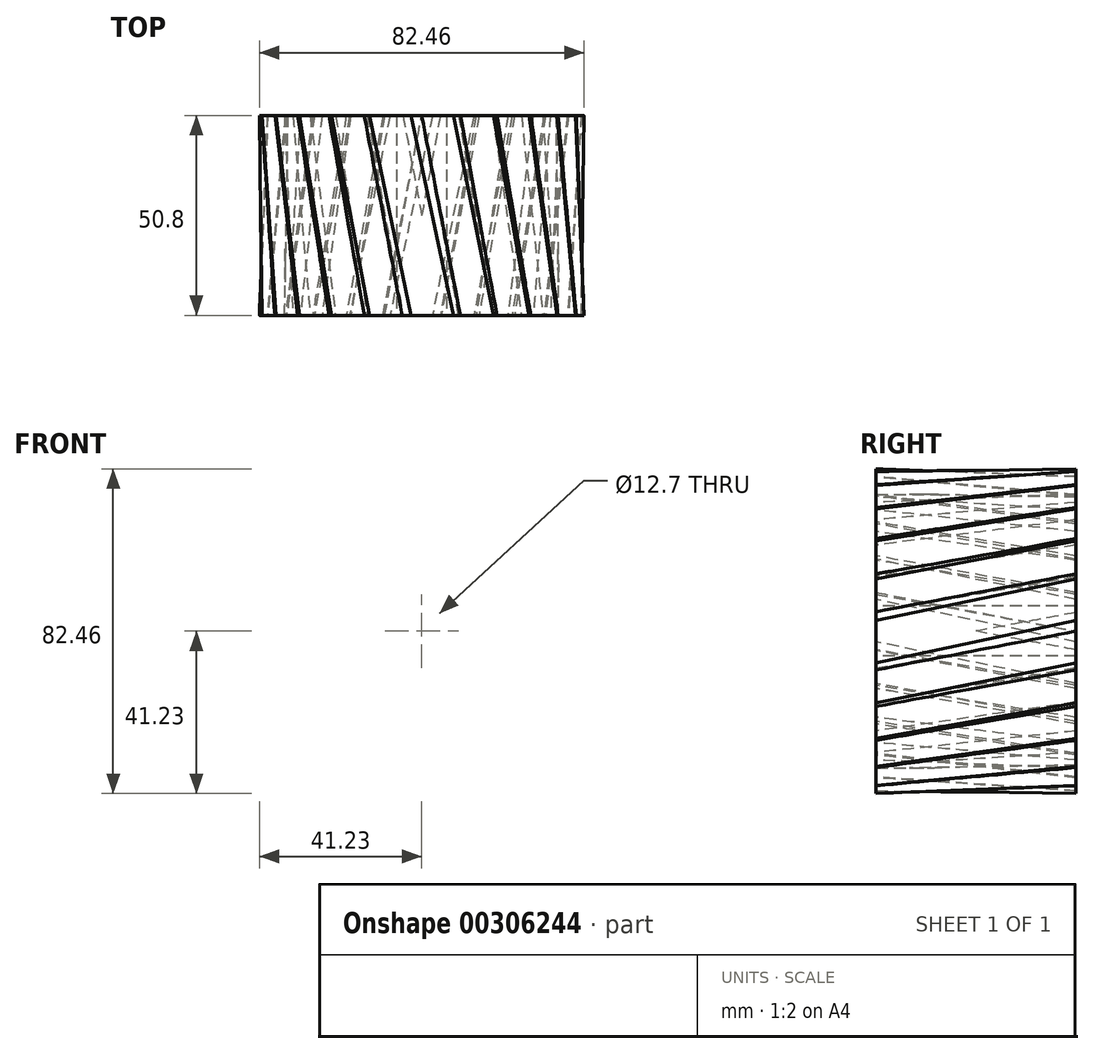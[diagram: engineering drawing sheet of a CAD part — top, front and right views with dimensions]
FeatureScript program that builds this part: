
annotation { "Feature Type Name" : "Feature", "Feature Type Description" : "" }
export const myFeature = defineFeature(function(context is Context, id is Id, definition is map)
    precondition{}
    {
        {
            var Q0;
            Q0=qCreatedBy(makeId("Front.planeOp"),FACE);
            cPlane(context, id + "F0", {"entities" : qUnion([Q0]), "cplaneType" : CPlaneType.OFFSET, "offset" : 50.8 * mm, "width" : 152.4 * mm, "height" : 152.4 * mm});
        }
        {
            var Q0;
            Q0=qCreatedBy(makeId("Front.planeOp"),FACE);
            var sketch = newSketch(context, id + "F1", { "sketchPlane" : qUnion([Q0])});
            skArc(sketch, "E0", {"start": v(-6.06, 34.4) * mm, "mid": v(-6.81, 34.25) * mm, "end": v(-7.56, 34.1) * mm});
            skArc(sketch, "E1.trimOffspring", {"start": v(-0.13, 38.41) * mm, "mid": v(-0.86, 39.8) * mm, "end": v(-1.82, 41.06) * mm});
            skLineSegment(sketch, "E2", {"start": v(0, 37.8) * mm, "end": v(0, 36.48) * mm});
            skLineSegment(sketch, "E3", {"start": v(-2.2, 41.23) * mm, "end": v(-2.7, 41.23) * mm});
            skLineSegment(sketch, "E4.MirrorCS", {"start": v(-3.2, 41.16) * mm, "end": v(-2.7, 41.23) * mm});
            skArc(sketch, "E5.MirrorCS", {"start": v(-4.89, 38.1) * mm, "mid": v(-4.34, 39.58) * mm, "end": v(-3.56, 40.95) * mm});
            skLineSegment(sketch, "E6.MirrorCS", {"start": v(-4.93, 37.47) * mm, "end": v(-4.76, 36.17) * mm});
            skPoint(sketch, "E7.visualSharp", {"position": v(0, 34.93) * mm});
            skArc(sketch, "E7.filletArc", {"start": v(0, 35.2) * mm, "mid": v(0.08, 35) * mm, "end": v(0.28, 34.92) * mm});
            skArc(sketch, "E8.filletArc", {"start": v(0, 36.48) * mm, "mid": v(0.44, 35.38) * mm, "end": v(1.52, 34.9) * mm});
            skPoint(sketch, "E9.visualSharp", {"position": v(-4.56, 34.63) * mm});
            skArc(sketch, "E9.filletArc", {"start": v(-6.06, 34.4) * mm, "mid": v(-5.06, 35.02) * mm, "end": v(-4.76, 36.17) * mm});
            skPoint(sketch, "E10.visualSharp", {"position": v(-4.97, 37.77) * mm});
            skArc(sketch, "E10.filletArc", {"start": v(-4.89, 38.1) * mm, "mid": v(-4.94, 37.79) * mm, "end": v(-4.93, 37.47) * mm});
            skPoint(sketch, "E11.visualSharp", {"position": v(0, 38.1) * mm});
            skArc(sketch, "E11.filletArc", {"start": v(0, 37.8) * mm, "mid": v(-0.03, 38.1) * mm, "end": v(-0.13, 38.41) * mm});
            skPoint(sketch, "E12.visualSharp", {"position": v(-3.43, 41.13) * mm});
            skArc(sketch, "E12.filletArc", {"start": v(-3.2, 41.16) * mm, "mid": v(-3.4, 41.1) * mm, "end": v(-3.56, 40.95) * mm});
            skPoint(sketch, "E13.visualSharp", {"position": v(-1.97, 41.23) * mm});
            skArc(sketch, "E13.filletArc", {"start": v(-1.82, 41.06) * mm, "mid": v(-1.99, 41.18) * mm, "end": v(-2.2, 41.23) * mm});
            skArc(sketch, "E14.1.0", {"start": v(-9.44, 35.24) * mm, "mid": v(-8.73, 34.29) * mm, "end": v(-7.56, 34.1) * mm});
            skLineSegment(sketch, "E14.1.1", {"start": v(-9.78, 36.5) * mm, "end": v(-9.44, 35.24) * mm});
            skLineSegment(sketch, "E14.1.2", {"start": v(-14.46, 34.91) * mm, "end": v(-13.96, 33.7) * mm});
            skLineSegment(sketch, "E14.1.3", {"start": v(-12.79, 39.26) * mm, "end": v(-13.28, 39.12) * mm});
            skPoint(sketch, "E14.1.4", {"position": v(-12.58, 39.31) * mm});
            skPoint(sketch, "E14.1.5", {"position": v(-13.96, 38.84) * mm});
            skLineSegment(sketch, "E14.1.6", {"start": v(-13.75, 38.93) * mm, "end": v(-13.28, 39.12) * mm});
            skArc(sketch, "E14.1.7", {"start": v(-10.06, 37.07) * mm, "mid": v(-11.14, 38.23) * mm, "end": v(-12.38, 39.2) * mm});
            skPoint(sketch, "E14.1.8", {"position": v(-9.86, 36.8) * mm});
            skArc(sketch, "E14.1.9", {"start": v(-14.58, 35.54) * mm, "mid": v(-14.44, 37.1) * mm, "end": v(-14.03, 38.63) * mm});
            skPoint(sketch, "E14.1.10", {"position": v(-14.58, 35.2) * mm});
            skArc(sketch, "E14.1.11", {"start": v(-14.58, 35.54) * mm, "mid": v(-14.55, 35.22) * mm, "end": v(-14.46, 34.91) * mm});
            skArc(sketch, "E14.1.12", {"start": v(-9.78, 36.5) * mm, "mid": v(-9.9, 36.8) * mm, "end": v(-10.06, 37.07) * mm});
            skArc(sketch, "E14.1.13", {"start": v(-12.38, 39.2) * mm, "mid": v(-12.58, 39.27) * mm, "end": v(-12.79, 39.26) * mm});
            skArc(sketch, "E14.1.14", {"start": v(-13.75, 38.93) * mm, "mid": v(-13.92, 38.8) * mm, "end": v(-14.03, 38.63) * mm});
            skArc(sketch, "E14.1.15", {"start": v(-14.76, 31.65) * mm, "mid": v(-13.95, 32.52) * mm, "end": v(-13.96, 33.7) * mm});
            skArc(sketch, "E14.2.0", {"start": v(-18.24, 31.6) * mm, "mid": v(-17.3, 30.86) * mm, "end": v(-16.13, 30.98) * mm});
            skLineSegment(sketch, "E14.2.1", {"start": v(-18.9, 32.73) * mm, "end": v(-18.24, 31.6) * mm});
            skLineSegment(sketch, "E14.2.2", {"start": v(-23, 29.98) * mm, "end": v(-22.2, 28.94) * mm});
            skLineSegment(sketch, "E14.2.3", {"start": v(-22.51, 34.6) * mm, "end": v(-22.95, 34.35) * mm});
            skPoint(sketch, "E14.2.4", {"position": v(-22.32, 34.72) * mm});
            skPoint(sketch, "E14.2.5", {"position": v(-23.53, 33.9) * mm});
            skLineSegment(sketch, "E14.2.6", {"start": v(-23.36, 34.04) * mm, "end": v(-22.95, 34.35) * mm});
            skArc(sketch, "E14.2.7", {"start": v(-19.32, 33.2) * mm, "mid": v(-20.65, 34.04) * mm, "end": v(-22.1, 34.65) * mm});
            skPoint(sketch, "E14.2.8", {"position": v(-19.05, 33) * mm});
            skArc(sketch, "E14.2.9", {"start": v(-23.28, 30.55) * mm, "mid": v(-23.55, 32.1) * mm, "end": v(-23.55, 33.68) * mm});
            skPoint(sketch, "E14.2.10", {"position": v(-23.2, 30.23) * mm});
            skArc(sketch, "E14.2.11", {"start": v(-23.28, 30.55) * mm, "mid": v(-23.17, 30.25) * mm, "end": v(-23, 29.98) * mm});
            skArc(sketch, "E14.2.12", {"start": v(-18.9, 32.73) * mm, "mid": v(-19.08, 32.99) * mm, "end": v(-19.32, 33.2) * mm});
            skArc(sketch, "E14.2.13", {"start": v(-22.1, 34.65) * mm, "mid": v(-22.31, 34.67) * mm, "end": v(-22.51, 34.6) * mm});
            skArc(sketch, "E14.2.14", {"start": v(-23.36, 34.04) * mm, "mid": v(-23.5, 33.88) * mm, "end": v(-23.55, 33.68) * mm});
            skArc(sketch, "E14.2.15", {"start": v(-22.45, 26.76) * mm, "mid": v(-21.89, 27.8) * mm, "end": v(-22.2, 28.94) * mm});
            skArc(sketch, "E15.3.3.0", {"start": v(-25.8, 25.8) * mm, "mid": v(-24.7, 25.33) * mm, "end": v(-23.6, 25.75) * mm});
            skLineSegment(sketch, "E15.4.3.0", {"start": v(-26.72, 26.72) * mm, "end": v(-25.8, 25.8) * mm});
            skLineSegment(sketch, "E15.7.3.0", {"start": v(-29.98, 23) * mm, "end": v(-28.94, 22.2) * mm});
            skLineSegment(sketch, "E15.10.3.0", {"start": v(-30.7, 27.6) * mm, "end": v(-31.06, 27.24) * mm});
            skPoint(sketch, "E15.13.3.0", {"position": v(-30.55, 27.76) * mm});
            skPoint(sketch, "E15.14.3.0", {"position": v(-31.5, 26.66) * mm});
            skLineSegment(sketch, "E15.15.3.0", {"start": v(-31.37, 26.84) * mm, "end": v(-31.06, 27.24) * mm});
            skArc(sketch, "E15.18.3.0", {"start": v(-27.25, 27.07) * mm, "mid": v(-28.76, 27.54) * mm, "end": v(-30.32, 27.75) * mm});
            skPoint(sketch, "E15.22.3.0", {"position": v(-26.94, 26.94) * mm});
            skArc(sketch, "E15.23.3.0", {"start": v(-30.4, 23.49) * mm, "mid": v(-31.06, 24.92) * mm, "end": v(-31.47, 26.44) * mm});
            skPoint(sketch, "E15.27.3.0", {"position": v(-30.23, 23.2) * mm});
            skArc(sketch, "E15.28.3.0", {"start": v(-30.4, 23.49) * mm, "mid": v(-30.21, 23.22) * mm, "end": v(-29.98, 23) * mm});
            skArc(sketch, "E15.32.3.0", {"start": v(-26.72, 26.72) * mm, "mid": v(-26.97, 26.92) * mm, "end": v(-27.25, 27.07) * mm});
            skArc(sketch, "E15.36.3.0", {"start": v(-30.32, 27.75) * mm, "mid": v(-30.53, 27.72) * mm, "end": v(-30.7, 27.6) * mm});
            skArc(sketch, "E15.40.3.0", {"start": v(-31.37, 26.84) * mm, "mid": v(-31.46, 26.65) * mm, "end": v(-31.47, 26.44) * mm});
            skArc(sketch, "E15.44.3.0", {"start": v(-28.6, 20.04) * mm, "mid": v(-28.34, 21.19) * mm, "end": v(-28.94, 22.2) * mm});
            skArc(sketch, "E15.3.4.0", {"start": v(-31.6, 18.24) * mm, "mid": v(-30.42, 18.07) * mm, "end": v(-29.46, 18.76) * mm});
            skLineSegment(sketch, "E15.4.4.0", {"start": v(-32.73, 18.9) * mm, "end": v(-31.6, 18.24) * mm});
            skLineSegment(sketch, "E15.7.4.0", {"start": v(-34.91, 14.46) * mm, "end": v(-33.7, 13.96) * mm});
            skLineSegment(sketch, "E15.10.4.0", {"start": v(-36.8, 18.71) * mm, "end": v(-37.06, 18.27) * mm});
            skPoint(sketch, "E15.13.4.0", {"position": v(-36.7, 18.9) * mm});
            skPoint(sketch, "E15.14.4.0", {"position": v(-37.33, 17.6) * mm});
            skLineSegment(sketch, "E15.15.4.0", {"start": v(-37.25, 17.8) * mm, "end": v(-37.06, 18.27) * mm});
            skArc(sketch, "E15.18.4.0", {"start": v(-33.33, 19.1) * mm, "mid": v(-34.9, 19.16) * mm, "end": v(-36.47, 18.96) * mm});
            skPoint(sketch, "E15.22.4.0", {"position": v(-33, 19.05) * mm});
            skArc(sketch, "E15.23.4.0", {"start": v(-35.44, 14.82) * mm, "mid": v(-36.45, 16.03) * mm, "end": v(-37.24, 17.4) * mm});
            skPoint(sketch, "E15.27.4.0", {"position": v(-35.2, 14.58) * mm});
            skArc(sketch, "E15.28.4.0", {"start": v(-35.44, 14.82) * mm, "mid": v(-35.2, 14.61) * mm, "end": v(-34.91, 14.46) * mm});
            skArc(sketch, "E15.32.4.0", {"start": v(-32.73, 18.9) * mm, "mid": v(-33.02, 19.03) * mm, "end": v(-33.33, 19.1) * mm});
            skArc(sketch, "E15.36.4.0", {"start": v(-36.47, 18.96) * mm, "mid": v(-36.66, 18.87) * mm, "end": v(-36.8, 18.71) * mm});
            skArc(sketch, "E15.40.4.0", {"start": v(-37.25, 17.8) * mm, "mid": v(-37.29, 17.6) * mm, "end": v(-37.24, 17.4) * mm});
            skArc(sketch, "E15.44.4.0", {"start": v(-32.82, 11.95) * mm, "mid": v(-32.86, 13.13) * mm, "end": v(-33.7, 13.96) * mm});
            skArc(sketch, "E15.3.5.0", {"start": v(-35.24, 9.44) * mm, "mid": v(-34.06, 9.58) * mm, "end": v(-33.31, 10.5) * mm});
            skLineSegment(sketch, "E15.4.5.0", {"start": v(-36.5, 9.78) * mm, "end": v(-35.24, 9.44) * mm});
            skLineSegment(sketch, "E15.7.5.0", {"start": v(-37.47, 4.93) * mm, "end": v(-36.17, 4.76) * mm});
            skLineSegment(sketch, "E15.10.5.0", {"start": v(-40.4, 8.55) * mm, "end": v(-40.52, 8.06) * mm});
            skPoint(sketch, "E15.13.5.0", {"position": v(-40.33, 8.77) * mm});
            skPoint(sketch, "E15.14.5.0", {"position": v(-40.62, 7.34) * mm});
            skLineSegment(sketch, "E15.15.5.0", {"start": v(-40.59, 7.56) * mm, "end": v(-40.52, 8.06) * mm});
            skArc(sketch, "E15.18.5.0", {"start": v(-37.14, 9.82) * mm, "mid": v(-38.67, 9.47) * mm, "end": v(-40.13, 8.87) * mm});
            skPoint(sketch, "E15.22.5.0", {"position": v(-36.8, 9.86) * mm});
            skArc(sketch, "E15.23.5.0", {"start": v(-38.07, 5.14) * mm, "mid": v(-39.35, 6.05) * mm, "end": v(-40.47, 7.16) * mm});
            skPoint(sketch, "E15.27.5.0", {"position": v(-37.77, 4.97) * mm});
            skArc(sketch, "E15.28.5.0", {"start": v(-38.07, 5.14) * mm, "mid": v(-37.78, 5) * mm, "end": v(-37.47, 4.93) * mm});
            skArc(sketch, "E15.32.5.0", {"start": v(-36.5, 9.78) * mm, "mid": v(-36.82, 9.83) * mm, "end": v(-37.14, 9.82) * mm});
            skArc(sketch, "E15.36.5.0", {"start": v(-40.13, 8.87) * mm, "mid": v(-40.3, 8.74) * mm, "end": v(-40.4, 8.55) * mm});
            skArc(sketch, "E15.40.5.0", {"start": v(-40.59, 7.56) * mm, "mid": v(-40.57, 7.35) * mm, "end": v(-40.47, 7.16) * mm});
            skArc(sketch, "E15.44.5.0", {"start": v(-34.8, 3.05) * mm, "mid": v(-35.13, 4.18) * mm, "end": v(-36.17, 4.76) * mm});
            skArc(sketch, "E15.3.6.0", {"start": v(-36.48, 0) * mm, "mid": v(-35.38, 0.44) * mm, "end": v(-34.9, 1.52) * mm});
            skLineSegment(sketch, "E15.4.6.0", {"start": v(-37.8, 0) * mm, "end": v(-36.48, 0) * mm});
            skLineSegment(sketch, "E15.7.6.0", {"start": v(-37.47, -4.93) * mm, "end": v(-36.17, -4.76) * mm});
            skLineSegment(sketch, "E15.10.6.0", {"start": v(-41.23, -2.2) * mm, "end": v(-41.23, -2.7) * mm});
            skPoint(sketch, "E15.13.6.0", {"position": v(-41.23, -1.97) * mm});
            skPoint(sketch, "E15.14.6.0", {"position": v(-41.13, -3.43) * mm});
            skLineSegment(sketch, "E15.15.6.0", {"start": v(-41.16, -3.2) * mm, "end": v(-41.23, -2.7) * mm});
            skArc(sketch, "E15.18.6.0", {"start": v(-38.41, -0.13) * mm, "mid": v(-39.8, -0.86) * mm, "end": v(-41.06, -1.82) * mm});
            skPoint(sketch, "E15.22.6.0", {"position": v(-38.1, 0) * mm});
            skArc(sketch, "E15.23.6.0", {"start": v(-38.1, -4.89) * mm, "mid": v(-39.58, -4.34) * mm, "end": v(-40.95, -3.56) * mm});
            skPoint(sketch, "E15.27.6.0", {"position": v(-37.77, -4.97) * mm});
            skArc(sketch, "E15.28.6.0", {"start": v(-38.1, -4.89) * mm, "mid": v(-37.79, -4.94) * mm, "end": v(-37.47, -4.93) * mm});
            skArc(sketch, "E15.32.6.0", {"start": v(-37.8, 0) * mm, "mid": v(-38.1, -0.03) * mm, "end": v(-38.41, -0.13) * mm});
            skArc(sketch, "E15.36.6.0", {"start": v(-41.06, -1.82) * mm, "mid": v(-41.18, -1.99) * mm, "end": v(-41.23, -2.2) * mm});
            skArc(sketch, "E15.40.6.0", {"start": v(-41.16, -3.2) * mm, "mid": v(-41.1, -3.4) * mm, "end": v(-40.95, -3.56) * mm});
            skArc(sketch, "E15.44.6.0", {"start": v(-34.4, -6.06) * mm, "mid": v(-35.02, -5.06) * mm, "end": v(-36.17, -4.76) * mm});
            skArc(sketch, "E15.3.7.0", {"start": v(-35.24, -9.44) * mm, "mid": v(-34.29, -8.73) * mm, "end": v(-34.1, -7.56) * mm});
            skLineSegment(sketch, "E15.4.7.0", {"start": v(-36.5, -9.78) * mm, "end": v(-35.24, -9.44) * mm});
            skLineSegment(sketch, "E15.7.7.0", {"start": v(-34.91, -14.46) * mm, "end": v(-33.7, -13.96) * mm});
            skLineSegment(sketch, "E15.10.7.0", {"start": v(-39.26, -12.79) * mm, "end": v(-39.12, -13.28) * mm});
            skPoint(sketch, "E15.13.7.0", {"position": v(-39.31, -12.58) * mm});
            skPoint(sketch, "E15.14.7.0", {"position": v(-38.84, -13.96) * mm});
            skLineSegment(sketch, "E15.15.7.0", {"start": v(-38.93, -13.75) * mm, "end": v(-39.12, -13.28) * mm});
            skArc(sketch, "E15.18.7.0", {"start": v(-37.07, -10.06) * mm, "mid": v(-38.23, -11.14) * mm, "end": v(-39.2, -12.38) * mm});
            skPoint(sketch, "E15.22.7.0", {"position": v(-36.8, -9.86) * mm});
            skArc(sketch, "E15.23.7.0", {"start": v(-35.54, -14.58) * mm, "mid": v(-37.1, -14.44) * mm, "end": v(-38.63, -14.03) * mm});
            skPoint(sketch, "E15.27.7.0", {"position": v(-35.2, -14.58) * mm});
            skArc(sketch, "E15.28.7.0", {"start": v(-35.54, -14.58) * mm, "mid": v(-35.22, -14.55) * mm, "end": v(-34.91, -14.46) * mm});
            skArc(sketch, "E15.32.7.0", {"start": v(-36.5, -9.78) * mm, "mid": v(-36.8, -9.9) * mm, "end": v(-37.07, -10.06) * mm});
            skArc(sketch, "E15.36.7.0", {"start": v(-39.2, -12.38) * mm, "mid": v(-39.27, -12.58) * mm, "end": v(-39.26, -12.79) * mm});
            skArc(sketch, "E15.40.7.0", {"start": v(-38.93, -13.75) * mm, "mid": v(-38.8, -13.92) * mm, "end": v(-38.63, -14.03) * mm});
            skArc(sketch, "E15.44.7.0", {"start": v(-31.65, -14.76) * mm, "mid": v(-32.52, -13.95) * mm, "end": v(-33.7, -13.96) * mm});
            skArc(sketch, "E15.3.8.0", {"start": v(-31.6, -18.24) * mm, "mid": v(-30.86, -17.3) * mm, "end": v(-30.98, -16.13) * mm});
            skLineSegment(sketch, "E15.4.8.0", {"start": v(-32.73, -18.9) * mm, "end": v(-31.6, -18.24) * mm});
            skLineSegment(sketch, "E15.7.8.0", {"start": v(-29.98, -23) * mm, "end": v(-28.94, -22.2) * mm});
            skLineSegment(sketch, "E15.10.8.0", {"start": v(-34.6, -22.51) * mm, "end": v(-34.35, -22.95) * mm});
            skPoint(sketch, "E15.13.8.0", {"position": v(-34.72, -22.32) * mm});
            skPoint(sketch, "E15.14.8.0", {"position": v(-33.9, -23.53) * mm});
            skLineSegment(sketch, "E15.15.8.0", {"start": v(-34.04, -23.36) * mm, "end": v(-34.35, -22.95) * mm});
            skArc(sketch, "E15.18.8.0", {"start": v(-33.2, -19.32) * mm, "mid": v(-34.04, -20.65) * mm, "end": v(-34.65, -22.1) * mm});
            skPoint(sketch, "E15.22.8.0", {"position": v(-33, -19.05) * mm});
            skArc(sketch, "E15.23.8.0", {"start": v(-30.55, -23.28) * mm, "mid": v(-32.1, -23.55) * mm, "end": v(-33.68, -23.55) * mm});
            skPoint(sketch, "E15.27.8.0", {"position": v(-30.23, -23.2) * mm});
            skArc(sketch, "E15.28.8.0", {"start": v(-30.55, -23.28) * mm, "mid": v(-30.25, -23.17) * mm, "end": v(-29.98, -23) * mm});
            skArc(sketch, "E15.32.8.0", {"start": v(-32.73, -18.9) * mm, "mid": v(-32.99, -19.08) * mm, "end": v(-33.2, -19.32) * mm});
            skArc(sketch, "E15.36.8.0", {"start": v(-34.65, -22.1) * mm, "mid": v(-34.67, -22.31) * mm, "end": v(-34.6, -22.51) * mm});
            skArc(sketch, "E15.40.8.0", {"start": v(-34.04, -23.36) * mm, "mid": v(-33.88, -23.5) * mm, "end": v(-33.68, -23.55) * mm});
            skArc(sketch, "E15.44.8.0", {"start": v(-26.76, -22.45) * mm, "mid": v(-27.8, -21.89) * mm, "end": v(-28.94, -22.2) * mm});
            skArc(sketch, "E15.3.9.0", {"start": v(-25.8, -25.8) * mm, "mid": v(-25.33, -24.7) * mm, "end": v(-25.75, -23.6) * mm});
            skLineSegment(sketch, "E15.4.9.0", {"start": v(-26.72, -26.72) * mm, "end": v(-25.8, -25.8) * mm});
            skLineSegment(sketch, "E15.7.9.0", {"start": v(-23, -29.98) * mm, "end": v(-22.2, -28.94) * mm});
            skLineSegment(sketch, "E15.10.9.0", {"start": v(-27.6, -30.7) * mm, "end": v(-27.24, -31.06) * mm});
            skPoint(sketch, "E15.13.9.0", {"position": v(-27.76, -30.55) * mm});
            skPoint(sketch, "E15.14.9.0", {"position": v(-26.66, -31.5) * mm});
            skLineSegment(sketch, "E15.15.9.0", {"start": v(-26.84, -31.37) * mm, "end": v(-27.24, -31.06) * mm});
            skArc(sketch, "E15.18.9.0", {"start": v(-27.07, -27.25) * mm, "mid": v(-27.54, -28.76) * mm, "end": v(-27.75, -30.32) * mm});
            skPoint(sketch, "E15.22.9.0", {"position": v(-26.94, -26.94) * mm});
            skArc(sketch, "E15.23.9.0", {"start": v(-23.49, -30.4) * mm, "mid": v(-24.92, -31.06) * mm, "end": v(-26.44, -31.47) * mm});
            skPoint(sketch, "E15.27.9.0", {"position": v(-23.2, -30.23) * mm});
            skArc(sketch, "E15.28.9.0", {"start": v(-23.49, -30.4) * mm, "mid": v(-23.22, -30.21) * mm, "end": v(-23, -29.98) * mm});
            skArc(sketch, "E15.32.9.0", {"start": v(-26.72, -26.72) * mm, "mid": v(-26.92, -26.97) * mm, "end": v(-27.07, -27.25) * mm});
            skArc(sketch, "E15.36.9.0", {"start": v(-27.75, -30.32) * mm, "mid": v(-27.72, -30.53) * mm, "end": v(-27.6, -30.7) * mm});
            skArc(sketch, "E15.40.9.0", {"start": v(-26.84, -31.37) * mm, "mid": v(-26.65, -31.46) * mm, "end": v(-26.44, -31.47) * mm});
            skArc(sketch, "E15.44.9.0", {"start": v(-20.04, -28.6) * mm, "mid": v(-21.19, -28.34) * mm, "end": v(-22.2, -28.94) * mm});
            skArc(sketch, "E15.3.10.0", {"start": v(-18.24, -31.6) * mm, "mid": v(-18.07, -30.42) * mm, "end": v(-18.76, -29.46) * mm});
            skLineSegment(sketch, "E15.4.10.0", {"start": v(-18.9, -32.73) * mm, "end": v(-18.24, -31.6) * mm});
            skLineSegment(sketch, "E15.7.10.0", {"start": v(-14.46, -34.91) * mm, "end": v(-13.96, -33.7) * mm});
            skLineSegment(sketch, "E15.10.10.0", {"start": v(-18.71, -36.8) * mm, "end": v(-18.27, -37.06) * mm});
            skPoint(sketch, "E15.13.10.0", {"position": v(-18.9, -36.7) * mm});
            skPoint(sketch, "E15.14.10.0", {"position": v(-17.6, -37.33) * mm});
            skLineSegment(sketch, "E15.15.10.0", {"start": v(-17.8, -37.25) * mm, "end": v(-18.27, -37.06) * mm});
            skArc(sketch, "E15.18.10.0", {"start": v(-19.1, -33.33) * mm, "mid": v(-19.16, -34.9) * mm, "end": v(-18.96, -36.47) * mm});
            skPoint(sketch, "E15.22.10.0", {"position": v(-19.05, -33) * mm});
            skArc(sketch, "E15.23.10.0", {"start": v(-14.82, -35.44) * mm, "mid": v(-16.03, -36.45) * mm, "end": v(-17.4, -37.24) * mm});
            skPoint(sketch, "E15.27.10.0", {"position": v(-14.58, -35.2) * mm});
            skArc(sketch, "E15.28.10.0", {"start": v(-14.82, -35.44) * mm, "mid": v(-14.61, -35.2) * mm, "end": v(-14.46, -34.91) * mm});
            skArc(sketch, "E15.32.10.0", {"start": v(-18.9, -32.73) * mm, "mid": v(-19.03, -33.02) * mm, "end": v(-19.1, -33.33) * mm});
            skArc(sketch, "E15.36.10.0", {"start": v(-18.96, -36.47) * mm, "mid": v(-18.87, -36.66) * mm, "end": v(-18.71, -36.8) * mm});
            skArc(sketch, "E15.40.10.0", {"start": v(-17.8, -37.25) * mm, "mid": v(-17.6, -37.29) * mm, "end": v(-17.4, -37.24) * mm});
            skArc(sketch, "E15.44.10.0", {"start": v(-11.95, -32.82) * mm, "mid": v(-13.13, -32.86) * mm, "end": v(-13.96, -33.7) * mm});
            skArc(sketch, "E15.3.11.0", {"start": v(-9.44, -35.24) * mm, "mid": v(-9.58, -34.06) * mm, "end": v(-10.5, -33.31) * mm});
            skLineSegment(sketch, "E15.4.11.0", {"start": v(-9.78, -36.5) * mm, "end": v(-9.44, -35.24) * mm});
            skLineSegment(sketch, "E15.7.11.0", {"start": v(-4.93, -37.47) * mm, "end": v(-4.76, -36.17) * mm});
            skLineSegment(sketch, "E15.10.11.0", {"start": v(-8.55, -40.4) * mm, "end": v(-8.06, -40.52) * mm});
            skPoint(sketch, "E15.13.11.0", {"position": v(-8.77, -40.33) * mm});
            skPoint(sketch, "E15.14.11.0", {"position": v(-7.34, -40.62) * mm});
            skLineSegment(sketch, "E15.15.11.0", {"start": v(-7.56, -40.59) * mm, "end": v(-8.06, -40.52) * mm});
            skArc(sketch, "E15.18.11.0", {"start": v(-9.82, -37.14) * mm, "mid": v(-9.47, -38.67) * mm, "end": v(-8.87, -40.13) * mm});
            skPoint(sketch, "E15.22.11.0", {"position": v(-9.86, -36.8) * mm});
            skArc(sketch, "E15.23.11.0", {"start": v(-5.14, -38.07) * mm, "mid": v(-6.05, -39.35) * mm, "end": v(-7.16, -40.47) * mm});
            skPoint(sketch, "E15.27.11.0", {"position": v(-4.97, -37.77) * mm});
            skArc(sketch, "E15.28.11.0", {"start": v(-5.14, -38.07) * mm, "mid": v(-5, -37.78) * mm, "end": v(-4.93, -37.47) * mm});
            skArc(sketch, "E15.32.11.0", {"start": v(-9.78, -36.5) * mm, "mid": v(-9.83, -36.82) * mm, "end": v(-9.82, -37.14) * mm});
            skArc(sketch, "E15.36.11.0", {"start": v(-8.87, -40.13) * mm, "mid": v(-8.74, -40.3) * mm, "end": v(-8.55, -40.4) * mm});
            skArc(sketch, "E15.40.11.0", {"start": v(-7.56, -40.59) * mm, "mid": v(-7.35, -40.57) * mm, "end": v(-7.16, -40.47) * mm});
            skArc(sketch, "E15.44.11.0", {"start": v(-3.05, -34.8) * mm, "mid": v(-4.18, -35.13) * mm, "end": v(-4.76, -36.17) * mm});
            skArc(sketch, "E15.3.12.0", {"start": v(0, -36.48) * mm, "mid": v(-0.44, -35.38) * mm, "end": v(-1.52, -34.9) * mm});
            skLineSegment(sketch, "E15.4.12.0", {"start": v(0, -37.8) * mm, "end": v(0, -36.48) * mm});
            skLineSegment(sketch, "E15.7.12.0", {"start": v(4.93, -37.47) * mm, "end": v(4.76, -36.17) * mm});
            skLineSegment(sketch, "E15.10.12.0", {"start": v(2.2, -41.23) * mm, "end": v(2.7, -41.23) * mm});
            skPoint(sketch, "E15.13.12.0", {"position": v(1.97, -41.23) * mm});
            skPoint(sketch, "E15.14.12.0", {"position": v(3.43, -41.13) * mm});
            skLineSegment(sketch, "E15.15.12.0", {"start": v(3.2, -41.16) * mm, "end": v(2.7, -41.23) * mm});
            skArc(sketch, "E15.18.12.0", {"start": v(0.13, -38.41) * mm, "mid": v(0.86, -39.8) * mm, "end": v(1.82, -41.06) * mm});
            skPoint(sketch, "E15.22.12.0", {"position": v(0, -38.1) * mm});
            skArc(sketch, "E15.23.12.0", {"start": v(4.89, -38.1) * mm, "mid": v(4.34, -39.58) * mm, "end": v(3.56, -40.95) * mm});
            skPoint(sketch, "E15.27.12.0", {"position": v(4.97, -37.77) * mm});
            skArc(sketch, "E15.28.12.0", {"start": v(4.89, -38.1) * mm, "mid": v(4.94, -37.79) * mm, "end": v(4.93, -37.47) * mm});
            skArc(sketch, "E15.32.12.0", {"start": v(0, -37.8) * mm, "mid": v(0.03, -38.1) * mm, "end": v(0.13, -38.41) * mm});
            skArc(sketch, "E15.36.12.0", {"start": v(1.82, -41.06) * mm, "mid": v(1.99, -41.18) * mm, "end": v(2.2, -41.23) * mm});
            skArc(sketch, "E15.40.12.0", {"start": v(3.2, -41.16) * mm, "mid": v(3.4, -41.1) * mm, "end": v(3.56, -40.95) * mm});
            skArc(sketch, "E15.44.12.0", {"start": v(6.06, -34.4) * mm, "mid": v(5.06, -35.02) * mm, "end": v(4.76, -36.17) * mm});
            skArc(sketch, "E15.3.13.0", {"start": v(9.44, -35.24) * mm, "mid": v(8.73, -34.29) * mm, "end": v(7.56, -34.1) * mm});
            skLineSegment(sketch, "E15.4.13.0", {"start": v(9.78, -36.5) * mm, "end": v(9.44, -35.24) * mm});
            skLineSegment(sketch, "E15.7.13.0", {"start": v(14.46, -34.91) * mm, "end": v(13.96, -33.7) * mm});
            skLineSegment(sketch, "E15.10.13.0", {"start": v(12.79, -39.26) * mm, "end": v(13.28, -39.12) * mm});
            skPoint(sketch, "E15.13.13.0", {"position": v(12.58, -39.31) * mm});
            skPoint(sketch, "E15.14.13.0", {"position": v(13.96, -38.84) * mm});
            skLineSegment(sketch, "E15.15.13.0", {"start": v(13.75, -38.93) * mm, "end": v(13.28, -39.12) * mm});
            skArc(sketch, "E15.18.13.0", {"start": v(10.06, -37.07) * mm, "mid": v(11.14, -38.23) * mm, "end": v(12.38, -39.2) * mm});
            skPoint(sketch, "E15.22.13.0", {"position": v(9.86, -36.8) * mm});
            skArc(sketch, "E15.23.13.0", {"start": v(14.58, -35.54) * mm, "mid": v(14.44, -37.1) * mm, "end": v(14.03, -38.63) * mm});
            skPoint(sketch, "E15.27.13.0", {"position": v(14.58, -35.2) * mm});
            skArc(sketch, "E15.28.13.0", {"start": v(14.58, -35.54) * mm, "mid": v(14.55, -35.22) * mm, "end": v(14.46, -34.91) * mm});
            skArc(sketch, "E15.32.13.0", {"start": v(9.78, -36.5) * mm, "mid": v(9.9, -36.8) * mm, "end": v(10.06, -37.07) * mm});
            skArc(sketch, "E15.36.13.0", {"start": v(12.38, -39.2) * mm, "mid": v(12.58, -39.27) * mm, "end": v(12.79, -39.26) * mm});
            skArc(sketch, "E15.40.13.0", {"start": v(13.75, -38.93) * mm, "mid": v(13.92, -38.8) * mm, "end": v(14.03, -38.63) * mm});
            skArc(sketch, "E15.44.13.0", {"start": v(14.76, -31.65) * mm, "mid": v(13.95, -32.52) * mm, "end": v(13.96, -33.7) * mm});
            skArc(sketch, "E15.3.14.0", {"start": v(18.24, -31.6) * mm, "mid": v(17.3, -30.86) * mm, "end": v(16.13, -30.98) * mm});
            skLineSegment(sketch, "E15.4.14.0", {"start": v(18.9, -32.73) * mm, "end": v(18.24, -31.6) * mm});
            skLineSegment(sketch, "E15.7.14.0", {"start": v(23, -29.98) * mm, "end": v(22.2, -28.94) * mm});
            skLineSegment(sketch, "E15.10.14.0", {"start": v(22.51, -34.6) * mm, "end": v(22.95, -34.35) * mm});
            skPoint(sketch, "E15.13.14.0", {"position": v(22.32, -34.72) * mm});
            skPoint(sketch, "E15.14.14.0", {"position": v(23.53, -33.9) * mm});
            skLineSegment(sketch, "E15.15.14.0", {"start": v(23.36, -34.04) * mm, "end": v(22.95, -34.35) * mm});
            skArc(sketch, "E15.18.14.0", {"start": v(19.32, -33.2) * mm, "mid": v(20.65, -34.04) * mm, "end": v(22.1, -34.65) * mm});
            skPoint(sketch, "E15.22.14.0", {"position": v(19.05, -33) * mm});
            skArc(sketch, "E15.23.14.0", {"start": v(23.28, -30.55) * mm, "mid": v(23.55, -32.1) * mm, "end": v(23.55, -33.68) * mm});
            skPoint(sketch, "E15.27.14.0", {"position": v(23.2, -30.23) * mm});
            skArc(sketch, "E15.28.14.0", {"start": v(23.28, -30.55) * mm, "mid": v(23.17, -30.25) * mm, "end": v(23, -29.98) * mm});
            skArc(sketch, "E15.32.14.0", {"start": v(18.9, -32.73) * mm, "mid": v(19.08, -32.99) * mm, "end": v(19.32, -33.2) * mm});
            skArc(sketch, "E15.36.14.0", {"start": v(22.1, -34.65) * mm, "mid": v(22.31, -34.67) * mm, "end": v(22.51, -34.6) * mm});
            skArc(sketch, "E15.40.14.0", {"start": v(23.36, -34.04) * mm, "mid": v(23.5, -33.88) * mm, "end": v(23.55, -33.68) * mm});
            skArc(sketch, "E15.44.14.0", {"start": v(22.45, -26.76) * mm, "mid": v(21.89, -27.8) * mm, "end": v(22.2, -28.94) * mm});
            skArc(sketch, "E15.3.15.0", {"start": v(25.8, -25.8) * mm, "mid": v(24.7, -25.33) * mm, "end": v(23.6, -25.75) * mm});
            skLineSegment(sketch, "E15.4.15.0", {"start": v(26.72, -26.72) * mm, "end": v(25.8, -25.8) * mm});
            skLineSegment(sketch, "E15.7.15.0", {"start": v(29.98, -23) * mm, "end": v(28.94, -22.2) * mm});
            skLineSegment(sketch, "E15.10.15.0", {"start": v(30.7, -27.6) * mm, "end": v(31.06, -27.24) * mm});
            skPoint(sketch, "E15.13.15.0", {"position": v(30.55, -27.76) * mm});
            skPoint(sketch, "E15.14.15.0", {"position": v(31.5, -26.66) * mm});
            skLineSegment(sketch, "E15.15.15.0", {"start": v(31.37, -26.84) * mm, "end": v(31.06, -27.24) * mm});
            skArc(sketch, "E15.18.15.0", {"start": v(27.25, -27.07) * mm, "mid": v(28.76, -27.54) * mm, "end": v(30.32, -27.75) * mm});
            skPoint(sketch, "E15.22.15.0", {"position": v(26.94, -26.94) * mm});
            skArc(sketch, "E15.23.15.0", {"start": v(30.4, -23.49) * mm, "mid": v(31.06, -24.92) * mm, "end": v(31.47, -26.44) * mm});
            skPoint(sketch, "E15.27.15.0", {"position": v(30.23, -23.2) * mm});
            skArc(sketch, "E15.28.15.0", {"start": v(30.4, -23.49) * mm, "mid": v(30.21, -23.22) * mm, "end": v(29.98, -23) * mm});
            skArc(sketch, "E15.32.15.0", {"start": v(26.72, -26.72) * mm, "mid": v(26.97, -26.92) * mm, "end": v(27.25, -27.07) * mm});
            skArc(sketch, "E15.36.15.0", {"start": v(30.32, -27.75) * mm, "mid": v(30.53, -27.72) * mm, "end": v(30.7, -27.6) * mm});
            skArc(sketch, "E15.40.15.0", {"start": v(31.37, -26.84) * mm, "mid": v(31.46, -26.65) * mm, "end": v(31.47, -26.44) * mm});
            skArc(sketch, "E15.44.15.0", {"start": v(28.6, -20.04) * mm, "mid": v(28.34, -21.19) * mm, "end": v(28.94, -22.2) * mm});
            skArc(sketch, "E15.3.16.0", {"start": v(31.6, -18.24) * mm, "mid": v(30.42, -18.07) * mm, "end": v(29.46, -18.76) * mm});
            skLineSegment(sketch, "E15.4.16.0", {"start": v(32.73, -18.9) * mm, "end": v(31.6, -18.24) * mm});
            skLineSegment(sketch, "E15.7.16.0", {"start": v(34.91, -14.46) * mm, "end": v(33.7, -13.96) * mm});
            skLineSegment(sketch, "E15.10.16.0", {"start": v(36.8, -18.71) * mm, "end": v(37.06, -18.27) * mm});
            skPoint(sketch, "E15.13.16.0", {"position": v(36.7, -18.9) * mm});
            skPoint(sketch, "E15.14.16.0", {"position": v(37.33, -17.6) * mm});
            skLineSegment(sketch, "E15.15.16.0", {"start": v(37.25, -17.8) * mm, "end": v(37.06, -18.27) * mm});
            skArc(sketch, "E15.18.16.0", {"start": v(33.33, -19.1) * mm, "mid": v(34.9, -19.16) * mm, "end": v(36.47, -18.96) * mm});
            skPoint(sketch, "E15.22.16.0", {"position": v(33, -19.05) * mm});
            skArc(sketch, "E15.23.16.0", {"start": v(35.44, -14.82) * mm, "mid": v(36.45, -16.03) * mm, "end": v(37.24, -17.4) * mm});
            skPoint(sketch, "E15.27.16.0", {"position": v(35.2, -14.58) * mm});
            skArc(sketch, "E15.28.16.0", {"start": v(35.44, -14.82) * mm, "mid": v(35.2, -14.61) * mm, "end": v(34.91, -14.46) * mm});
            skArc(sketch, "E15.32.16.0", {"start": v(32.73, -18.9) * mm, "mid": v(33.02, -19.03) * mm, "end": v(33.33, -19.1) * mm});
            skArc(sketch, "E15.36.16.0", {"start": v(36.47, -18.96) * mm, "mid": v(36.66, -18.87) * mm, "end": v(36.8, -18.71) * mm});
            skArc(sketch, "E15.40.16.0", {"start": v(37.25, -17.8) * mm, "mid": v(37.29, -17.6) * mm, "end": v(37.24, -17.4) * mm});
            skArc(sketch, "E15.44.16.0", {"start": v(32.82, -11.95) * mm, "mid": v(32.86, -13.13) * mm, "end": v(33.7, -13.96) * mm});
            skArc(sketch, "E15.3.17.0", {"start": v(35.24, -9.44) * mm, "mid": v(34.06, -9.58) * mm, "end": v(33.31, -10.5) * mm});
            skLineSegment(sketch, "E15.4.17.0", {"start": v(36.5, -9.78) * mm, "end": v(35.24, -9.44) * mm});
            skLineSegment(sketch, "E15.7.17.0", {"start": v(37.47, -4.93) * mm, "end": v(36.17, -4.76) * mm});
            skLineSegment(sketch, "E15.10.17.0", {"start": v(40.4, -8.55) * mm, "end": v(40.52, -8.06) * mm});
            skPoint(sketch, "E15.13.17.0", {"position": v(40.33, -8.77) * mm});
            skPoint(sketch, "E15.14.17.0", {"position": v(40.62, -7.34) * mm});
            skLineSegment(sketch, "E15.15.17.0", {"start": v(40.59, -7.56) * mm, "end": v(40.52, -8.06) * mm});
            skArc(sketch, "E15.18.17.0", {"start": v(37.14, -9.82) * mm, "mid": v(38.67, -9.47) * mm, "end": v(40.13, -8.87) * mm});
            skPoint(sketch, "E15.22.17.0", {"position": v(36.8, -9.86) * mm});
            skArc(sketch, "E15.23.17.0", {"start": v(38.07, -5.14) * mm, "mid": v(39.35, -6.05) * mm, "end": v(40.47, -7.16) * mm});
            skPoint(sketch, "E15.27.17.0", {"position": v(37.77, -4.97) * mm});
            skArc(sketch, "E15.28.17.0", {"start": v(38.07, -5.14) * mm, "mid": v(37.78, -5) * mm, "end": v(37.47, -4.93) * mm});
            skArc(sketch, "E15.32.17.0", {"start": v(36.5, -9.78) * mm, "mid": v(36.82, -9.83) * mm, "end": v(37.14, -9.82) * mm});
            skArc(sketch, "E15.36.17.0", {"start": v(40.13, -8.87) * mm, "mid": v(40.3, -8.74) * mm, "end": v(40.4, -8.55) * mm});
            skArc(sketch, "E15.40.17.0", {"start": v(40.59, -7.56) * mm, "mid": v(40.57, -7.35) * mm, "end": v(40.47, -7.16) * mm});
            skArc(sketch, "E15.44.17.0", {"start": v(34.8, -3.05) * mm, "mid": v(35.13, -4.18) * mm, "end": v(36.17, -4.76) * mm});
            skArc(sketch, "E15.3.18.0", {"start": v(36.48, 0) * mm, "mid": v(35.38, -0.44) * mm, "end": v(34.9, -1.52) * mm});
            skLineSegment(sketch, "E15.4.18.0", {"start": v(37.8, 0) * mm, "end": v(36.48, 0) * mm});
            skLineSegment(sketch, "E15.7.18.0", {"start": v(37.47, 4.93) * mm, "end": v(36.17, 4.76) * mm});
            skLineSegment(sketch, "E15.10.18.0", {"start": v(41.23, 2.2) * mm, "end": v(41.23, 2.7) * mm});
            skPoint(sketch, "E15.13.18.0", {"position": v(41.23, 1.97) * mm});
            skPoint(sketch, "E15.14.18.0", {"position": v(41.13, 3.43) * mm});
            skLineSegment(sketch, "E15.15.18.0", {"start": v(41.16, 3.2) * mm, "end": v(41.23, 2.7) * mm});
            skArc(sketch, "E15.18.18.0", {"start": v(38.41, 0.13) * mm, "mid": v(39.8, 0.86) * mm, "end": v(41.06, 1.82) * mm});
            skPoint(sketch, "E15.22.18.0", {"position": v(38.1, 0) * mm});
            skArc(sketch, "E15.23.18.0", {"start": v(38.1, 4.89) * mm, "mid": v(39.58, 4.34) * mm, "end": v(40.95, 3.56) * mm});
            skPoint(sketch, "E15.27.18.0", {"position": v(37.77, 4.97) * mm});
            skArc(sketch, "E15.28.18.0", {"start": v(38.1, 4.89) * mm, "mid": v(37.79, 4.94) * mm, "end": v(37.47, 4.93) * mm});
            skArc(sketch, "E15.32.18.0", {"start": v(37.8, 0) * mm, "mid": v(38.1, 0.03) * mm, "end": v(38.41, 0.13) * mm});
            skArc(sketch, "E15.36.18.0", {"start": v(41.06, 1.82) * mm, "mid": v(41.18, 1.99) * mm, "end": v(41.23, 2.2) * mm});
            skArc(sketch, "E15.40.18.0", {"start": v(41.16, 3.2) * mm, "mid": v(41.1, 3.4) * mm, "end": v(40.95, 3.56) * mm});
            skArc(sketch, "E15.44.18.0", {"start": v(34.4, 6.06) * mm, "mid": v(35.02, 5.06) * mm, "end": v(36.17, 4.76) * mm});
            skArc(sketch, "E15.3.19.0", {"start": v(35.24, 9.44) * mm, "mid": v(34.29, 8.73) * mm, "end": v(34.1, 7.56) * mm});
            skLineSegment(sketch, "E15.4.19.0", {"start": v(36.5, 9.78) * mm, "end": v(35.24, 9.44) * mm});
            skLineSegment(sketch, "E15.7.19.0", {"start": v(34.91, 14.46) * mm, "end": v(33.7, 13.96) * mm});
            skLineSegment(sketch, "E15.10.19.0", {"start": v(39.26, 12.79) * mm, "end": v(39.12, 13.28) * mm});
            skPoint(sketch, "E15.13.19.0", {"position": v(39.31, 12.58) * mm});
            skPoint(sketch, "E15.14.19.0", {"position": v(38.84, 13.96) * mm});
            skLineSegment(sketch, "E15.15.19.0", {"start": v(38.93, 13.75) * mm, "end": v(39.12, 13.28) * mm});
            skArc(sketch, "E15.18.19.0", {"start": v(37.07, 10.06) * mm, "mid": v(38.23, 11.14) * mm, "end": v(39.2, 12.38) * mm});
            skPoint(sketch, "E15.22.19.0", {"position": v(36.8, 9.86) * mm});
            skArc(sketch, "E15.23.19.0", {"start": v(35.54, 14.58) * mm, "mid": v(37.1, 14.44) * mm, "end": v(38.63, 14.03) * mm});
            skPoint(sketch, "E15.27.19.0", {"position": v(35.2, 14.58) * mm});
            skArc(sketch, "E15.28.19.0", {"start": v(35.54, 14.58) * mm, "mid": v(35.22, 14.55) * mm, "end": v(34.91, 14.46) * mm});
            skArc(sketch, "E15.32.19.0", {"start": v(36.5, 9.78) * mm, "mid": v(36.8, 9.9) * mm, "end": v(37.07, 10.06) * mm});
            skArc(sketch, "E15.36.19.0", {"start": v(39.2, 12.38) * mm, "mid": v(39.27, 12.58) * mm, "end": v(39.26, 12.79) * mm});
            skArc(sketch, "E15.40.19.0", {"start": v(38.93, 13.75) * mm, "mid": v(38.8, 13.92) * mm, "end": v(38.63, 14.03) * mm});
            skArc(sketch, "E15.44.19.0", {"start": v(31.65, 14.76) * mm, "mid": v(32.52, 13.95) * mm, "end": v(33.7, 13.96) * mm});
            skArc(sketch, "E15.3.20.0", {"start": v(31.6, 18.24) * mm, "mid": v(30.86, 17.3) * mm, "end": v(30.98, 16.13) * mm});
            skLineSegment(sketch, "E15.4.20.0", {"start": v(32.73, 18.9) * mm, "end": v(31.6, 18.24) * mm});
            skLineSegment(sketch, "E15.7.20.0", {"start": v(29.98, 23) * mm, "end": v(28.94, 22.2) * mm});
            skLineSegment(sketch, "E15.10.20.0", {"start": v(34.6, 22.51) * mm, "end": v(34.35, 22.95) * mm});
            skPoint(sketch, "E15.13.20.0", {"position": v(34.72, 22.32) * mm});
            skPoint(sketch, "E15.14.20.0", {"position": v(33.9, 23.53) * mm});
            skLineSegment(sketch, "E15.15.20.0", {"start": v(34.04, 23.36) * mm, "end": v(34.35, 22.95) * mm});
            skArc(sketch, "E15.18.20.0", {"start": v(33.2, 19.32) * mm, "mid": v(34.04, 20.65) * mm, "end": v(34.65, 22.1) * mm});
            skPoint(sketch, "E15.22.20.0", {"position": v(33, 19.05) * mm});
            skArc(sketch, "E15.23.20.0", {"start": v(30.55, 23.28) * mm, "mid": v(32.1, 23.55) * mm, "end": v(33.68, 23.55) * mm});
            skPoint(sketch, "E15.27.20.0", {"position": v(30.23, 23.2) * mm});
            skArc(sketch, "E15.28.20.0", {"start": v(30.55, 23.28) * mm, "mid": v(30.25, 23.17) * mm, "end": v(29.98, 23) * mm});
            skArc(sketch, "E15.32.20.0", {"start": v(32.73, 18.9) * mm, "mid": v(32.99, 19.08) * mm, "end": v(33.2, 19.32) * mm});
            skArc(sketch, "E15.36.20.0", {"start": v(34.65, 22.1) * mm, "mid": v(34.67, 22.31) * mm, "end": v(34.6, 22.51) * mm});
            skArc(sketch, "E15.40.20.0", {"start": v(34.04, 23.36) * mm, "mid": v(33.88, 23.5) * mm, "end": v(33.68, 23.55) * mm});
            skArc(sketch, "E15.44.20.0", {"start": v(26.76, 22.45) * mm, "mid": v(27.8, 21.89) * mm, "end": v(28.94, 22.2) * mm});
            skArc(sketch, "E15.3.21.0", {"start": v(25.8, 25.8) * mm, "mid": v(25.33, 24.7) * mm, "end": v(25.75, 23.6) * mm});
            skLineSegment(sketch, "E15.4.21.0", {"start": v(26.72, 26.72) * mm, "end": v(25.8, 25.8) * mm});
            skLineSegment(sketch, "E15.7.21.0", {"start": v(23, 29.98) * mm, "end": v(22.2, 28.94) * mm});
            skLineSegment(sketch, "E15.10.21.0", {"start": v(27.6, 30.7) * mm, "end": v(27.24, 31.06) * mm});
            skPoint(sketch, "E15.13.21.0", {"position": v(27.76, 30.55) * mm});
            skPoint(sketch, "E15.14.21.0", {"position": v(26.66, 31.5) * mm});
            skLineSegment(sketch, "E15.15.21.0", {"start": v(26.84, 31.37) * mm, "end": v(27.24, 31.06) * mm});
            skArc(sketch, "E15.18.21.0", {"start": v(27.07, 27.25) * mm, "mid": v(27.54, 28.76) * mm, "end": v(27.75, 30.32) * mm});
            skPoint(sketch, "E15.22.21.0", {"position": v(26.94, 26.94) * mm});
            skArc(sketch, "E15.23.21.0", {"start": v(23.49, 30.4) * mm, "mid": v(24.92, 31.06) * mm, "end": v(26.44, 31.47) * mm});
            skPoint(sketch, "E15.27.21.0", {"position": v(23.2, 30.23) * mm});
            skArc(sketch, "E15.28.21.0", {"start": v(23.49, 30.4) * mm, "mid": v(23.22, 30.21) * mm, "end": v(23, 29.98) * mm});
            skArc(sketch, "E15.32.21.0", {"start": v(26.72, 26.72) * mm, "mid": v(26.92, 26.97) * mm, "end": v(27.07, 27.25) * mm});
            skArc(sketch, "E15.36.21.0", {"start": v(27.75, 30.32) * mm, "mid": v(27.72, 30.53) * mm, "end": v(27.6, 30.7) * mm});
            skArc(sketch, "E15.40.21.0", {"start": v(26.84, 31.37) * mm, "mid": v(26.65, 31.46) * mm, "end": v(26.44, 31.47) * mm});
            skArc(sketch, "E15.44.21.0", {"start": v(20.04, 28.6) * mm, "mid": v(21.19, 28.34) * mm, "end": v(22.2, 28.94) * mm});
            skArc(sketch, "E15.3.22.0", {"start": v(18.24, 31.6) * mm, "mid": v(18.07, 30.42) * mm, "end": v(18.76, 29.46) * mm});
            skLineSegment(sketch, "E15.4.22.0", {"start": v(18.9, 32.73) * mm, "end": v(18.24, 31.6) * mm});
            skLineSegment(sketch, "E15.7.22.0", {"start": v(14.46, 34.91) * mm, "end": v(13.96, 33.7) * mm});
            skLineSegment(sketch, "E15.10.22.0", {"start": v(18.71, 36.8) * mm, "end": v(18.27, 37.06) * mm});
            skPoint(sketch, "E15.13.22.0", {"position": v(18.9, 36.7) * mm});
            skPoint(sketch, "E15.14.22.0", {"position": v(17.6, 37.33) * mm});
            skLineSegment(sketch, "E15.15.22.0", {"start": v(17.8, 37.25) * mm, "end": v(18.27, 37.06) * mm});
            skArc(sketch, "E15.18.22.0", {"start": v(19.1, 33.33) * mm, "mid": v(19.16, 34.9) * mm, "end": v(18.96, 36.47) * mm});
            skPoint(sketch, "E15.22.22.0", {"position": v(19.05, 33) * mm});
            skArc(sketch, "E15.23.22.0", {"start": v(14.82, 35.44) * mm, "mid": v(16.03, 36.45) * mm, "end": v(17.4, 37.24) * mm});
            skPoint(sketch, "E15.27.22.0", {"position": v(14.58, 35.2) * mm});
            skArc(sketch, "E15.28.22.0", {"start": v(14.82, 35.44) * mm, "mid": v(14.61, 35.2) * mm, "end": v(14.46, 34.91) * mm});
            skArc(sketch, "E15.32.22.0", {"start": v(18.9, 32.73) * mm, "mid": v(19.03, 33.02) * mm, "end": v(19.1, 33.33) * mm});
            skArc(sketch, "E15.36.22.0", {"start": v(18.96, 36.47) * mm, "mid": v(18.87, 36.66) * mm, "end": v(18.71, 36.8) * mm});
            skArc(sketch, "E15.40.22.0", {"start": v(17.8, 37.25) * mm, "mid": v(17.6, 37.29) * mm, "end": v(17.4, 37.24) * mm});
            skArc(sketch, "E15.44.22.0", {"start": v(11.95, 32.82) * mm, "mid": v(13.13, 32.86) * mm, "end": v(13.96, 33.7) * mm});
            skArc(sketch, "E15.3.23.0", {"start": v(9.44, 35.24) * mm, "mid": v(9.58, 34.06) * mm, "end": v(10.5, 33.31) * mm});
            skLineSegment(sketch, "E15.4.23.0", {"start": v(9.78, 36.5) * mm, "end": v(9.44, 35.24) * mm});
            skLineSegment(sketch, "E15.7.23.0", {"start": v(4.93, 37.47) * mm, "end": v(4.76, 36.17) * mm});
            skLineSegment(sketch, "E15.10.23.0", {"start": v(8.55, 40.4) * mm, "end": v(8.06, 40.52) * mm});
            skPoint(sketch, "E15.13.23.0", {"position": v(8.77, 40.33) * mm});
            skPoint(sketch, "E15.14.23.0", {"position": v(7.34, 40.62) * mm});
            skLineSegment(sketch, "E15.15.23.0", {"start": v(7.56, 40.59) * mm, "end": v(8.06, 40.52) * mm});
            skArc(sketch, "E15.18.23.0", {"start": v(9.82, 37.14) * mm, "mid": v(9.47, 38.67) * mm, "end": v(8.87, 40.13) * mm});
            skPoint(sketch, "E15.22.23.0", {"position": v(9.86, 36.8) * mm});
            skArc(sketch, "E15.23.23.0", {"start": v(5.14, 38.07) * mm, "mid": v(6.05, 39.35) * mm, "end": v(7.16, 40.47) * mm});
            skPoint(sketch, "E15.27.23.0", {"position": v(4.97, 37.77) * mm});
            skArc(sketch, "E15.28.23.0", {"start": v(5.14, 38.07) * mm, "mid": v(5, 37.78) * mm, "end": v(4.93, 37.47) * mm});
            skArc(sketch, "E15.32.23.0", {"start": v(9.78, 36.5) * mm, "mid": v(9.83, 36.82) * mm, "end": v(9.82, 37.14) * mm});
            skArc(sketch, "E15.36.23.0", {"start": v(8.87, 40.13) * mm, "mid": v(8.74, 40.3) * mm, "end": v(8.55, 40.4) * mm});
            skArc(sketch, "E15.40.23.0", {"start": v(7.56, 40.59) * mm, "mid": v(7.35, 40.57) * mm, "end": v(7.16, 40.47) * mm});
            skArc(sketch, "E15.44.23.0", {"start": v(3.05, 34.8) * mm, "mid": v(4.18, 35.13) * mm, "end": v(4.76, 36.17) * mm});
            skArc(sketch, "E16.trimOffspring", {"start": v(3.05, 34.8) * mm, "mid": v(2.28, 34.85) * mm, "end": v(1.52, 34.9) * mm});
            skArc(sketch, "E17.trimOffspring", {"start": v(11.95, 32.82) * mm, "mid": v(11.23, 33.07) * mm, "end": v(10.5, 33.31) * mm});
            skArc(sketch, "E18.trimOffspring", {"start": v(20.04, 28.6) * mm, "mid": v(19.4, 29.04) * mm, "end": v(18.76, 29.46) * mm});
            skArc(sketch, "E19.trimOffspring", {"start": v(26.76, 22.45) * mm, "mid": v(26.26, 23.03) * mm, "end": v(25.75, 23.6) * mm});
            skArc(sketch, "E20.trimOffspring", {"start": v(31.65, 14.76) * mm, "mid": v(31.32, 15.45) * mm, "end": v(30.98, 16.13) * mm});
            skArc(sketch, "E21.trimOffspring", {"start": v(34.4, 6.06) * mm, "mid": v(34.25, 6.81) * mm, "end": v(34.1, 7.56) * mm});
            skArc(sketch, "E22.trimOffspring", {"start": v(34.8, -3.05) * mm, "mid": v(34.85, -2.28) * mm, "end": v(34.9, -1.52) * mm});
            skArc(sketch, "E23.trimOffspring", {"start": v(32.82, -11.95) * mm, "mid": v(33.07, -11.23) * mm, "end": v(33.31, -10.5) * mm});
            skArc(sketch, "E24.trimOffspring", {"start": v(28.6, -20.04) * mm, "mid": v(29.04, -19.4) * mm, "end": v(29.46, -18.76) * mm});
            skArc(sketch, "E25.trimOffspring", {"start": v(22.45, -26.76) * mm, "mid": v(23.03, -26.26) * mm, "end": v(23.6, -25.75) * mm});
            skArc(sketch, "E26.trimOffspring", {"start": v(14.76, -31.65) * mm, "mid": v(15.45, -31.32) * mm, "end": v(16.13, -30.98) * mm});
            skArc(sketch, "E27.trimOffspring", {"start": v(6.06, -34.4) * mm, "mid": v(6.81, -34.25) * mm, "end": v(7.56, -34.1) * mm});
            skArc(sketch, "E28.trimOffspring", {"start": v(-3.05, -34.8) * mm, "mid": v(-2.28, -34.85) * mm, "end": v(-1.52, -34.9) * mm});
            skArc(sketch, "E29.trimOffspring", {"start": v(-11.95, -32.82) * mm, "mid": v(-11.23, -33.07) * mm, "end": v(-10.5, -33.31) * mm});
            skArc(sketch, "E30.trimOffspring", {"start": v(-20.04, -28.6) * mm, "mid": v(-19.4, -29.04) * mm, "end": v(-18.76, -29.46) * mm});
            skArc(sketch, "E31.trimOffspring", {"start": v(-26.76, -22.45) * mm, "mid": v(-26.26, -23.03) * mm, "end": v(-25.75, -23.6) * mm});
            skArc(sketch, "E32.trimOffspring", {"start": v(-31.65, -14.76) * mm, "mid": v(-31.32, -15.45) * mm, "end": v(-30.98, -16.13) * mm});
            skArc(sketch, "E33.trimOffspring", {"start": v(-34.4, -6.06) * mm, "mid": v(-34.25, -6.81) * mm, "end": v(-34.1, -7.56) * mm});
            skArc(sketch, "E34.trimOffspring", {"start": v(-34.8, 3.05) * mm, "mid": v(-34.85, 2.28) * mm, "end": v(-34.9, 1.52) * mm});
            skArc(sketch, "E35.trimOffspring", {"start": v(-32.82, 11.95) * mm, "mid": v(-33.07, 11.23) * mm, "end": v(-33.31, 10.5) * mm});
            skArc(sketch, "E36.trimOffspring", {"start": v(-28.6, 20.04) * mm, "mid": v(-29.04, 19.4) * mm, "end": v(-29.46, 18.76) * mm});
            skArc(sketch, "E37.trimOffspring", {"start": v(-22.45, 26.76) * mm, "mid": v(-23.03, 26.26) * mm, "end": v(-23.6, 25.75) * mm});
            skArc(sketch, "E38.trimOffspring", {"start": v(-14.76, 31.65) * mm, "mid": v(-15.45, 31.32) * mm, "end": v(-16.13, 30.98) * mm});
            skSolve(sketch);
        }
        {
            var Q0;
            Q0=qCreatedBy(id+"F0.planeOp",FACE);
            var sketch = newSketch(context, id + "F2", { "sketchPlane" : qUnion([Q0])});
            skArc(sketch, "E39", {"start": v(-31.65, -14.76) * mm, "mid": v(-31.32, -15.45) * mm, "end": v(-30.98, -16.13) * mm});
            skArc(sketch, "E40.trimOffspring", {"start": v(-37.07, -10.06) * mm, "mid": v(-38.23, -11.14) * mm, "end": v(-39.2, -12.38) * mm});
            skLineSegment(sketch, "E41", {"start": v(-39.26, -12.79) * mm, "end": v(-39.12, -13.28) * mm});
            skLineSegment(sketch, "E42", {"start": v(-36.5, -9.78) * mm, "end": v(-35.24, -9.44) * mm});
            skLineSegment(sketch, "E43.MirrorCS", {"start": v(-38.93, -13.75) * mm, "end": v(-39.12, -13.28) * mm});
            skArc(sketch, "E44.MirrorCS", {"start": v(-35.54, -14.58) * mm, "mid": v(-37.1, -14.44) * mm, "end": v(-38.63, -14.03) * mm});
            skLineSegment(sketch, "E45.MirrorCS", {"start": v(-34.91, -14.46) * mm, "end": v(-33.7, -13.96) * mm});
            skPoint(sketch, "E46.visualSharp", {"position": v(-32.27, -13.37) * mm});
            skArc(sketch, "E46.filletArc", {"start": v(-32.07, -13.83) * mm, "mid": v(-32.35, -13.56) * mm, "end": v(-32.73, -13.56) * mm});
            skArc(sketch, "E47.filletArc", {"start": v(-31.65, -14.76) * mm, "mid": v(-32.52, -13.95) * mm, "end": v(-33.7, -13.96) * mm});
            skPoint(sketch, "E48.visualSharp", {"position": v(-33.73, -9.04) * mm});
            skArc(sketch, "E48.filletArc", {"start": v(-35.24, -9.44) * mm, "mid": v(-34.29, -8.73) * mm, "end": v(-34.1, -7.56) * mm});
            skPoint(sketch, "E49.visualSharp", {"position": v(-36.8, -9.86) * mm});
            skArc(sketch, "E49.filletArc", {"start": v(-36.5, -9.78) * mm, "mid": v(-36.8, -9.9) * mm, "end": v(-37.07, -10.06) * mm});
            skPoint(sketch, "E50.visualSharp", {"position": v(-35.2, -14.58) * mm});
            skArc(sketch, "E50.filletArc", {"start": v(-35.54, -14.58) * mm, "mid": v(-35.22, -14.55) * mm, "end": v(-34.91, -14.46) * mm});
            skPoint(sketch, "E51.visualSharp", {"position": v(-38.84, -13.96) * mm});
            skArc(sketch, "E51.filletArc", {"start": v(-38.93, -13.75) * mm, "mid": v(-38.8, -13.92) * mm, "end": v(-38.63, -14.03) * mm});
            skPoint(sketch, "E52.visualSharp", {"position": v(-39.31, -12.58) * mm});
            skArc(sketch, "E52.filletArc", {"start": v(-39.2, -12.38) * mm, "mid": v(-39.27, -12.58) * mm, "end": v(-39.26, -12.79) * mm});
            skArc(sketch, "E53.1.0", {"start": v(-26.76, -22.45) * mm, "mid": v(-27.8, -21.89) * mm, "end": v(-28.94, -22.2) * mm});
            skLineSegment(sketch, "E53.1.1", {"start": v(-29.98, -23) * mm, "end": v(-28.94, -22.2) * mm});
            skPoint(sketch, "E53.1.2", {"position": v(-30.23, -23.2) * mm});
            skArc(sketch, "E53.1.3", {"start": v(-30.55, -23.28) * mm, "mid": v(-32.1, -23.55) * mm, "end": v(-33.68, -23.55) * mm});
            skPoint(sketch, "E53.1.4", {"position": v(-33.9, -23.53) * mm});
            skPoint(sketch, "E53.1.5", {"position": v(-33, -19.05) * mm});
            skLineSegment(sketch, "E53.1.6", {"start": v(-32.73, -18.9) * mm, "end": v(-31.6, -18.24) * mm});
            skArc(sketch, "E53.1.7", {"start": v(-33.2, -19.32) * mm, "mid": v(-34.04, -20.65) * mm, "end": v(-34.65, -22.1) * mm});
            skPoint(sketch, "E53.1.8", {"position": v(-34.72, -22.32) * mm});
            skArc(sketch, "E53.1.9", {"start": v(-32.73, -18.9) * mm, "mid": v(-32.99, -19.08) * mm, "end": v(-33.2, -19.32) * mm});
            skArc(sketch, "E53.1.10", {"start": v(-34.04, -23.36) * mm, "mid": v(-33.88, -23.5) * mm, "end": v(-33.68, -23.55) * mm});
            skLineSegment(sketch, "E53.1.11", {"start": v(-34.6, -22.51) * mm, "end": v(-34.35, -22.95) * mm});
            skArc(sketch, "E53.1.12", {"start": v(-34.65, -22.1) * mm, "mid": v(-34.67, -22.31) * mm, "end": v(-34.6, -22.51) * mm});
            skArc(sketch, "E53.1.13", {"start": v(-31.6, -18.24) * mm, "mid": v(-30.86, -17.3) * mm, "end": v(-30.98, -16.13) * mm});
            skLineSegment(sketch, "E53.1.14", {"start": v(-34.04, -23.36) * mm, "end": v(-34.35, -22.95) * mm});
            skArc(sketch, "E53.1.15", {"start": v(-30.55, -23.28) * mm, "mid": v(-30.25, -23.17) * mm, "end": v(-29.98, -23) * mm});
            skArc(sketch, "E53.2.0", {"start": v(-20.04, -28.6) * mm, "mid": v(-21.19, -28.34) * mm, "end": v(-22.2, -28.94) * mm});
            skLineSegment(sketch, "E53.2.1", {"start": v(-23, -29.98) * mm, "end": v(-22.2, -28.94) * mm});
            skPoint(sketch, "E53.2.2", {"position": v(-23.2, -30.23) * mm});
            skArc(sketch, "E53.2.3", {"start": v(-23.49, -30.4) * mm, "mid": v(-24.92, -31.06) * mm, "end": v(-26.44, -31.47) * mm});
            skPoint(sketch, "E53.2.4", {"position": v(-26.66, -31.5) * mm});
            skPoint(sketch, "E53.2.5", {"position": v(-26.94, -26.94) * mm});
            skLineSegment(sketch, "E53.2.6", {"start": v(-26.72, -26.72) * mm, "end": v(-25.8, -25.8) * mm});
            skArc(sketch, "E53.2.7", {"start": v(-27.07, -27.25) * mm, "mid": v(-27.54, -28.76) * mm, "end": v(-27.75, -30.32) * mm});
            skPoint(sketch, "E53.2.8", {"position": v(-27.76, -30.55) * mm});
            skArc(sketch, "E53.2.9", {"start": v(-26.72, -26.72) * mm, "mid": v(-26.92, -26.97) * mm, "end": v(-27.07, -27.25) * mm});
            skArc(sketch, "E53.2.10", {"start": v(-26.84, -31.37) * mm, "mid": v(-26.65, -31.46) * mm, "end": v(-26.44, -31.47) * mm});
            skLineSegment(sketch, "E53.2.11", {"start": v(-27.6, -30.7) * mm, "end": v(-27.24, -31.06) * mm});
            skArc(sketch, "E53.2.12", {"start": v(-27.75, -30.32) * mm, "mid": v(-27.72, -30.53) * mm, "end": v(-27.6, -30.7) * mm});
            skArc(sketch, "E53.2.13", {"start": v(-25.8, -25.8) * mm, "mid": v(-25.33, -24.7) * mm, "end": v(-25.75, -23.6) * mm});
            skLineSegment(sketch, "E53.2.14", {"start": v(-26.84, -31.37) * mm, "end": v(-27.24, -31.06) * mm});
            skArc(sketch, "E53.2.15", {"start": v(-23.49, -30.4) * mm, "mid": v(-23.22, -30.21) * mm, "end": v(-23, -29.98) * mm});
            skArc(sketch, "E54.1.3.0", {"start": v(-11.95, -32.82) * mm, "mid": v(-13.13, -32.86) * mm, "end": v(-13.96, -33.7) * mm});
            skLineSegment(sketch, "E54.4.3.0", {"start": v(-14.46, -34.91) * mm, "end": v(-13.96, -33.7) * mm});
            skPoint(sketch, "E54.7.3.0", {"position": v(-14.58, -35.2) * mm});
            skArc(sketch, "E54.8.3.0", {"start": v(-14.82, -35.44) * mm, "mid": v(-16.03, -36.45) * mm, "end": v(-17.4, -37.24) * mm});
            skPoint(sketch, "E54.12.3.0", {"position": v(-17.6, -37.33) * mm});
            skPoint(sketch, "E54.13.3.0", {"position": v(-19.05, -33) * mm});
            skLineSegment(sketch, "E54.14.3.0", {"start": v(-18.9, -32.73) * mm, "end": v(-18.24, -31.6) * mm});
            skArc(sketch, "E54.17.3.0", {"start": v(-19.1, -33.33) * mm, "mid": v(-19.16, -34.9) * mm, "end": v(-18.96, -36.47) * mm});
            skPoint(sketch, "E54.21.3.0", {"position": v(-18.9, -36.7) * mm});
            skArc(sketch, "E54.22.3.0", {"start": v(-18.9, -32.73) * mm, "mid": v(-19.03, -33.02) * mm, "end": v(-19.1, -33.33) * mm});
            skArc(sketch, "E54.26.3.0", {"start": v(-17.8, -37.25) * mm, "mid": v(-17.6, -37.29) * mm, "end": v(-17.4, -37.24) * mm});
            skLineSegment(sketch, "E54.30.3.0", {"start": v(-18.71, -36.8) * mm, "end": v(-18.27, -37.06) * mm});
            skArc(sketch, "E54.33.3.0", {"start": v(-18.96, -36.47) * mm, "mid": v(-18.87, -36.66) * mm, "end": v(-18.71, -36.8) * mm});
            skArc(sketch, "E54.37.3.0", {"start": v(-18.24, -31.6) * mm, "mid": v(-18.07, -30.42) * mm, "end": v(-18.76, -29.46) * mm});
            skLineSegment(sketch, "E54.41.3.0", {"start": v(-17.8, -37.25) * mm, "end": v(-18.27, -37.06) * mm});
            skArc(sketch, "E54.44.3.0", {"start": v(-14.82, -35.44) * mm, "mid": v(-14.61, -35.2) * mm, "end": v(-14.46, -34.91) * mm});
            skArc(sketch, "E54.1.4.0", {"start": v(-3.05, -34.8) * mm, "mid": v(-4.18, -35.13) * mm, "end": v(-4.76, -36.17) * mm});
            skLineSegment(sketch, "E54.4.4.0", {"start": v(-4.93, -37.47) * mm, "end": v(-4.76, -36.17) * mm});
            skPoint(sketch, "E54.7.4.0", {"position": v(-4.97, -37.77) * mm});
            skArc(sketch, "E54.8.4.0", {"start": v(-5.14, -38.07) * mm, "mid": v(-6.05, -39.35) * mm, "end": v(-7.16, -40.47) * mm});
            skPoint(sketch, "E54.12.4.0", {"position": v(-7.34, -40.62) * mm});
            skPoint(sketch, "E54.13.4.0", {"position": v(-9.86, -36.8) * mm});
            skLineSegment(sketch, "E54.14.4.0", {"start": v(-9.78, -36.5) * mm, "end": v(-9.44, -35.24) * mm});
            skArc(sketch, "E54.17.4.0", {"start": v(-9.82, -37.14) * mm, "mid": v(-9.47, -38.67) * mm, "end": v(-8.87, -40.13) * mm});
            skPoint(sketch, "E54.21.4.0", {"position": v(-8.77, -40.33) * mm});
            skArc(sketch, "E54.22.4.0", {"start": v(-9.78, -36.5) * mm, "mid": v(-9.83, -36.82) * mm, "end": v(-9.82, -37.14) * mm});
            skArc(sketch, "E54.26.4.0", {"start": v(-7.56, -40.59) * mm, "mid": v(-7.35, -40.57) * mm, "end": v(-7.16, -40.47) * mm});
            skLineSegment(sketch, "E54.30.4.0", {"start": v(-8.55, -40.4) * mm, "end": v(-8.06, -40.52) * mm});
            skArc(sketch, "E54.33.4.0", {"start": v(-8.87, -40.13) * mm, "mid": v(-8.74, -40.3) * mm, "end": v(-8.55, -40.4) * mm});
            skArc(sketch, "E54.37.4.0", {"start": v(-9.44, -35.24) * mm, "mid": v(-9.58, -34.06) * mm, "end": v(-10.5, -33.31) * mm});
            skLineSegment(sketch, "E54.41.4.0", {"start": v(-7.56, -40.59) * mm, "end": v(-8.06, -40.52) * mm});
            skArc(sketch, "E54.44.4.0", {"start": v(-5.14, -38.07) * mm, "mid": v(-5, -37.78) * mm, "end": v(-4.93, -37.47) * mm});
            skArc(sketch, "E54.1.5.0", {"start": v(6.06, -34.4) * mm, "mid": v(5.06, -35.02) * mm, "end": v(4.76, -36.17) * mm});
            skLineSegment(sketch, "E54.4.5.0", {"start": v(4.93, -37.47) * mm, "end": v(4.76, -36.17) * mm});
            skPoint(sketch, "E54.7.5.0", {"position": v(4.97, -37.77) * mm});
            skArc(sketch, "E54.8.5.0", {"start": v(4.89, -38.1) * mm, "mid": v(4.34, -39.58) * mm, "end": v(3.56, -40.95) * mm});
            skPoint(sketch, "E54.12.5.0", {"position": v(3.43, -41.13) * mm});
            skPoint(sketch, "E54.13.5.0", {"position": v(0, -38.1) * mm});
            skLineSegment(sketch, "E54.14.5.0", {"start": v(0, -37.8) * mm, "end": v(0, -36.48) * mm});
            skArc(sketch, "E54.17.5.0", {"start": v(0.13, -38.41) * mm, "mid": v(0.86, -39.8) * mm, "end": v(1.82, -41.06) * mm});
            skPoint(sketch, "E54.21.5.0", {"position": v(1.97, -41.23) * mm});
            skArc(sketch, "E54.22.5.0", {"start": v(0, -37.8) * mm, "mid": v(0.03, -38.1) * mm, "end": v(0.13, -38.41) * mm});
            skArc(sketch, "E54.26.5.0", {"start": v(3.2, -41.16) * mm, "mid": v(3.4, -41.1) * mm, "end": v(3.56, -40.95) * mm});
            skLineSegment(sketch, "E54.30.5.0", {"start": v(2.2, -41.23) * mm, "end": v(2.7, -41.23) * mm});
            skArc(sketch, "E54.33.5.0", {"start": v(1.82, -41.06) * mm, "mid": v(1.99, -41.18) * mm, "end": v(2.2, -41.23) * mm});
            skArc(sketch, "E54.37.5.0", {"start": v(0, -36.48) * mm, "mid": v(-0.44, -35.38) * mm, "end": v(-1.52, -34.9) * mm});
            skLineSegment(sketch, "E54.41.5.0", {"start": v(3.2, -41.16) * mm, "end": v(2.7, -41.23) * mm});
            skArc(sketch, "E54.44.5.0", {"start": v(4.89, -38.1) * mm, "mid": v(4.94, -37.79) * mm, "end": v(4.93, -37.47) * mm});
            skArc(sketch, "E54.1.6.0", {"start": v(14.76, -31.65) * mm, "mid": v(13.95, -32.52) * mm, "end": v(13.96, -33.7) * mm});
            skLineSegment(sketch, "E54.4.6.0", {"start": v(14.46, -34.91) * mm, "end": v(13.96, -33.7) * mm});
            skPoint(sketch, "E54.7.6.0", {"position": v(14.58, -35.2) * mm});
            skArc(sketch, "E54.8.6.0", {"start": v(14.58, -35.54) * mm, "mid": v(14.44, -37.1) * mm, "end": v(14.03, -38.63) * mm});
            skPoint(sketch, "E54.12.6.0", {"position": v(13.96, -38.84) * mm});
            skPoint(sketch, "E54.13.6.0", {"position": v(9.86, -36.8) * mm});
            skLineSegment(sketch, "E54.14.6.0", {"start": v(9.78, -36.5) * mm, "end": v(9.44, -35.24) * mm});
            skArc(sketch, "E54.17.6.0", {"start": v(10.06, -37.07) * mm, "mid": v(11.14, -38.23) * mm, "end": v(12.38, -39.2) * mm});
            skPoint(sketch, "E54.21.6.0", {"position": v(12.58, -39.31) * mm});
            skArc(sketch, "E54.22.6.0", {"start": v(9.78, -36.5) * mm, "mid": v(9.9, -36.8) * mm, "end": v(10.06, -37.07) * mm});
            skArc(sketch, "E54.26.6.0", {"start": v(13.75, -38.93) * mm, "mid": v(13.92, -38.8) * mm, "end": v(14.03, -38.63) * mm});
            skLineSegment(sketch, "E54.30.6.0", {"start": v(12.79, -39.26) * mm, "end": v(13.28, -39.12) * mm});
            skArc(sketch, "E54.33.6.0", {"start": v(12.38, -39.2) * mm, "mid": v(12.58, -39.27) * mm, "end": v(12.79, -39.26) * mm});
            skArc(sketch, "E54.37.6.0", {"start": v(9.44, -35.24) * mm, "mid": v(8.73, -34.29) * mm, "end": v(7.56, -34.1) * mm});
            skLineSegment(sketch, "E54.41.6.0", {"start": v(13.75, -38.93) * mm, "end": v(13.28, -39.12) * mm});
            skArc(sketch, "E54.44.6.0", {"start": v(14.58, -35.54) * mm, "mid": v(14.55, -35.22) * mm, "end": v(14.46, -34.91) * mm});
            skArc(sketch, "E54.1.7.0", {"start": v(22.45, -26.76) * mm, "mid": v(21.89, -27.8) * mm, "end": v(22.2, -28.94) * mm});
            skLineSegment(sketch, "E54.4.7.0", {"start": v(23, -29.98) * mm, "end": v(22.2, -28.94) * mm});
            skPoint(sketch, "E54.7.7.0", {"position": v(23.2, -30.23) * mm});
            skArc(sketch, "E54.8.7.0", {"start": v(23.28, -30.55) * mm, "mid": v(23.55, -32.1) * mm, "end": v(23.55, -33.68) * mm});
            skPoint(sketch, "E54.12.7.0", {"position": v(23.53, -33.9) * mm});
            skPoint(sketch, "E54.13.7.0", {"position": v(19.05, -33) * mm});
            skLineSegment(sketch, "E54.14.7.0", {"start": v(18.9, -32.73) * mm, "end": v(18.24, -31.6) * mm});
            skArc(sketch, "E54.17.7.0", {"start": v(19.32, -33.2) * mm, "mid": v(20.65, -34.04) * mm, "end": v(22.1, -34.65) * mm});
            skPoint(sketch, "E54.21.7.0", {"position": v(22.32, -34.72) * mm});
            skArc(sketch, "E54.22.7.0", {"start": v(18.9, -32.73) * mm, "mid": v(19.08, -32.99) * mm, "end": v(19.32, -33.2) * mm});
            skArc(sketch, "E54.26.7.0", {"start": v(23.36, -34.04) * mm, "mid": v(23.5, -33.88) * mm, "end": v(23.55, -33.68) * mm});
            skLineSegment(sketch, "E54.30.7.0", {"start": v(22.51, -34.6) * mm, "end": v(22.95, -34.35) * mm});
            skArc(sketch, "E54.33.7.0", {"start": v(22.1, -34.65) * mm, "mid": v(22.31, -34.67) * mm, "end": v(22.51, -34.6) * mm});
            skArc(sketch, "E54.37.7.0", {"start": v(18.24, -31.6) * mm, "mid": v(17.3, -30.86) * mm, "end": v(16.13, -30.98) * mm});
            skLineSegment(sketch, "E54.41.7.0", {"start": v(23.36, -34.04) * mm, "end": v(22.95, -34.35) * mm});
            skArc(sketch, "E54.44.7.0", {"start": v(23.28, -30.55) * mm, "mid": v(23.17, -30.25) * mm, "end": v(23, -29.98) * mm});
            skArc(sketch, "E54.1.8.0", {"start": v(28.6, -20.04) * mm, "mid": v(28.34, -21.19) * mm, "end": v(28.94, -22.2) * mm});
            skLineSegment(sketch, "E54.4.8.0", {"start": v(29.98, -23) * mm, "end": v(28.94, -22.2) * mm});
            skPoint(sketch, "E54.7.8.0", {"position": v(30.23, -23.2) * mm});
            skArc(sketch, "E54.8.8.0", {"start": v(30.4, -23.49) * mm, "mid": v(31.06, -24.92) * mm, "end": v(31.47, -26.44) * mm});
            skPoint(sketch, "E54.12.8.0", {"position": v(31.5, -26.66) * mm});
            skPoint(sketch, "E54.13.8.0", {"position": v(26.94, -26.94) * mm});
            skLineSegment(sketch, "E54.14.8.0", {"start": v(26.72, -26.72) * mm, "end": v(25.8, -25.8) * mm});
            skArc(sketch, "E54.17.8.0", {"start": v(27.25, -27.07) * mm, "mid": v(28.76, -27.54) * mm, "end": v(30.32, -27.75) * mm});
            skPoint(sketch, "E54.21.8.0", {"position": v(30.55, -27.76) * mm});
            skArc(sketch, "E54.22.8.0", {"start": v(26.72, -26.72) * mm, "mid": v(26.97, -26.92) * mm, "end": v(27.25, -27.07) * mm});
            skArc(sketch, "E54.26.8.0", {"start": v(31.37, -26.84) * mm, "mid": v(31.46, -26.65) * mm, "end": v(31.47, -26.44) * mm});
            skLineSegment(sketch, "E54.30.8.0", {"start": v(30.7, -27.6) * mm, "end": v(31.06, -27.24) * mm});
            skArc(sketch, "E54.33.8.0", {"start": v(30.32, -27.75) * mm, "mid": v(30.53, -27.72) * mm, "end": v(30.7, -27.6) * mm});
            skArc(sketch, "E54.37.8.0", {"start": v(25.8, -25.8) * mm, "mid": v(24.7, -25.33) * mm, "end": v(23.6, -25.75) * mm});
            skLineSegment(sketch, "E54.41.8.0", {"start": v(31.37, -26.84) * mm, "end": v(31.06, -27.24) * mm});
            skArc(sketch, "E54.44.8.0", {"start": v(30.4, -23.49) * mm, "mid": v(30.21, -23.22) * mm, "end": v(29.98, -23) * mm});
            skArc(sketch, "E54.1.9.0", {"start": v(32.82, -11.95) * mm, "mid": v(32.86, -13.13) * mm, "end": v(33.7, -13.96) * mm});
            skLineSegment(sketch, "E54.4.9.0", {"start": v(34.91, -14.46) * mm, "end": v(33.7, -13.96) * mm});
            skPoint(sketch, "E54.7.9.0", {"position": v(35.2, -14.58) * mm});
            skArc(sketch, "E54.8.9.0", {"start": v(35.44, -14.82) * mm, "mid": v(36.45, -16.03) * mm, "end": v(37.24, -17.4) * mm});
            skPoint(sketch, "E54.12.9.0", {"position": v(37.33, -17.6) * mm});
            skPoint(sketch, "E54.13.9.0", {"position": v(33, -19.05) * mm});
            skLineSegment(sketch, "E54.14.9.0", {"start": v(32.73, -18.9) * mm, "end": v(31.6, -18.24) * mm});
            skArc(sketch, "E54.17.9.0", {"start": v(33.33, -19.1) * mm, "mid": v(34.9, -19.16) * mm, "end": v(36.47, -18.96) * mm});
            skPoint(sketch, "E54.21.9.0", {"position": v(36.7, -18.9) * mm});
            skArc(sketch, "E54.22.9.0", {"start": v(32.73, -18.9) * mm, "mid": v(33.02, -19.03) * mm, "end": v(33.33, -19.1) * mm});
            skArc(sketch, "E54.26.9.0", {"start": v(37.25, -17.8) * mm, "mid": v(37.29, -17.6) * mm, "end": v(37.24, -17.4) * mm});
            skLineSegment(sketch, "E54.30.9.0", {"start": v(36.8, -18.71) * mm, "end": v(37.06, -18.27) * mm});
            skArc(sketch, "E54.33.9.0", {"start": v(36.47, -18.96) * mm, "mid": v(36.66, -18.87) * mm, "end": v(36.8, -18.71) * mm});
            skArc(sketch, "E54.37.9.0", {"start": v(31.6, -18.24) * mm, "mid": v(30.42, -18.07) * mm, "end": v(29.46, -18.76) * mm});
            skLineSegment(sketch, "E54.41.9.0", {"start": v(37.25, -17.8) * mm, "end": v(37.06, -18.27) * mm});
            skArc(sketch, "E54.44.9.0", {"start": v(35.44, -14.82) * mm, "mid": v(35.2, -14.61) * mm, "end": v(34.91, -14.46) * mm});
            skArc(sketch, "E54.1.10.0", {"start": v(34.8, -3.05) * mm, "mid": v(35.13, -4.18) * mm, "end": v(36.17, -4.76) * mm});
            skLineSegment(sketch, "E54.4.10.0", {"start": v(37.47, -4.93) * mm, "end": v(36.17, -4.76) * mm});
            skPoint(sketch, "E54.7.10.0", {"position": v(37.77, -4.97) * mm});
            skArc(sketch, "E54.8.10.0", {"start": v(38.07, -5.14) * mm, "mid": v(39.35, -6.05) * mm, "end": v(40.47, -7.16) * mm});
            skPoint(sketch, "E54.12.10.0", {"position": v(40.62, -7.34) * mm});
            skPoint(sketch, "E54.13.10.0", {"position": v(36.8, -9.86) * mm});
            skLineSegment(sketch, "E54.14.10.0", {"start": v(36.5, -9.78) * mm, "end": v(35.24, -9.44) * mm});
            skArc(sketch, "E54.17.10.0", {"start": v(37.14, -9.82) * mm, "mid": v(38.67, -9.47) * mm, "end": v(40.13, -8.87) * mm});
            skPoint(sketch, "E54.21.10.0", {"position": v(40.33, -8.77) * mm});
            skArc(sketch, "E54.22.10.0", {"start": v(36.5, -9.78) * mm, "mid": v(36.82, -9.83) * mm, "end": v(37.14, -9.82) * mm});
            skArc(sketch, "E54.26.10.0", {"start": v(40.59, -7.56) * mm, "mid": v(40.57, -7.35) * mm, "end": v(40.47, -7.16) * mm});
            skLineSegment(sketch, "E54.30.10.0", {"start": v(40.4, -8.55) * mm, "end": v(40.52, -8.06) * mm});
            skArc(sketch, "E54.33.10.0", {"start": v(40.13, -8.87) * mm, "mid": v(40.3, -8.74) * mm, "end": v(40.4, -8.55) * mm});
            skArc(sketch, "E54.37.10.0", {"start": v(35.24, -9.44) * mm, "mid": v(34.06, -9.58) * mm, "end": v(33.31, -10.5) * mm});
            skLineSegment(sketch, "E54.41.10.0", {"start": v(40.59, -7.56) * mm, "end": v(40.52, -8.06) * mm});
            skArc(sketch, "E54.44.10.0", {"start": v(38.07, -5.14) * mm, "mid": v(37.78, -5) * mm, "end": v(37.47, -4.93) * mm});
            skArc(sketch, "E54.1.11.0", {"start": v(34.4, 6.06) * mm, "mid": v(35.02, 5.06) * mm, "end": v(36.17, 4.76) * mm});
            skLineSegment(sketch, "E54.4.11.0", {"start": v(37.47, 4.93) * mm, "end": v(36.17, 4.76) * mm});
            skPoint(sketch, "E54.7.11.0", {"position": v(37.77, 4.97) * mm});
            skArc(sketch, "E54.8.11.0", {"start": v(38.1, 4.89) * mm, "mid": v(39.58, 4.34) * mm, "end": v(40.95, 3.56) * mm});
            skPoint(sketch, "E54.12.11.0", {"position": v(41.13, 3.43) * mm});
            skPoint(sketch, "E54.13.11.0", {"position": v(38.1, 0) * mm});
            skLineSegment(sketch, "E54.14.11.0", {"start": v(37.8, 0) * mm, "end": v(36.48, 0) * mm});
            skArc(sketch, "E54.17.11.0", {"start": v(38.41, 0.13) * mm, "mid": v(39.8, 0.86) * mm, "end": v(41.06, 1.82) * mm});
            skPoint(sketch, "E54.21.11.0", {"position": v(41.23, 1.97) * mm});
            skArc(sketch, "E54.22.11.0", {"start": v(37.8, 0) * mm, "mid": v(38.1, 0.03) * mm, "end": v(38.41, 0.13) * mm});
            skArc(sketch, "E54.26.11.0", {"start": v(41.16, 3.2) * mm, "mid": v(41.1, 3.4) * mm, "end": v(40.95, 3.56) * mm});
            skLineSegment(sketch, "E54.30.11.0", {"start": v(41.23, 2.2) * mm, "end": v(41.23, 2.7) * mm});
            skArc(sketch, "E54.33.11.0", {"start": v(41.06, 1.82) * mm, "mid": v(41.18, 1.99) * mm, "end": v(41.23, 2.2) * mm});
            skArc(sketch, "E54.37.11.0", {"start": v(36.48, 0) * mm, "mid": v(35.38, -0.44) * mm, "end": v(34.9, -1.52) * mm});
            skLineSegment(sketch, "E54.41.11.0", {"start": v(41.16, 3.2) * mm, "end": v(41.23, 2.7) * mm});
            skArc(sketch, "E54.44.11.0", {"start": v(38.1, 4.89) * mm, "mid": v(37.79, 4.94) * mm, "end": v(37.47, 4.93) * mm});
            skArc(sketch, "E54.1.12.0", {"start": v(31.65, 14.76) * mm, "mid": v(32.52, 13.95) * mm, "end": v(33.7, 13.96) * mm});
            skLineSegment(sketch, "E54.4.12.0", {"start": v(34.91, 14.46) * mm, "end": v(33.7, 13.96) * mm});
            skPoint(sketch, "E54.7.12.0", {"position": v(35.2, 14.58) * mm});
            skArc(sketch, "E54.8.12.0", {"start": v(35.54, 14.58) * mm, "mid": v(37.1, 14.44) * mm, "end": v(38.63, 14.03) * mm});
            skPoint(sketch, "E54.12.12.0", {"position": v(38.84, 13.96) * mm});
            skPoint(sketch, "E54.13.12.0", {"position": v(36.8, 9.86) * mm});
            skLineSegment(sketch, "E54.14.12.0", {"start": v(36.5, 9.78) * mm, "end": v(35.24, 9.44) * mm});
            skArc(sketch, "E54.17.12.0", {"start": v(37.07, 10.06) * mm, "mid": v(38.23, 11.14) * mm, "end": v(39.2, 12.38) * mm});
            skPoint(sketch, "E54.21.12.0", {"position": v(39.31, 12.58) * mm});
            skArc(sketch, "E54.22.12.0", {"start": v(36.5, 9.78) * mm, "mid": v(36.8, 9.9) * mm, "end": v(37.07, 10.06) * mm});
            skArc(sketch, "E54.26.12.0", {"start": v(38.93, 13.75) * mm, "mid": v(38.8, 13.92) * mm, "end": v(38.63, 14.03) * mm});
            skLineSegment(sketch, "E54.30.12.0", {"start": v(39.26, 12.79) * mm, "end": v(39.12, 13.28) * mm});
            skArc(sketch, "E54.33.12.0", {"start": v(39.2, 12.38) * mm, "mid": v(39.27, 12.58) * mm, "end": v(39.26, 12.79) * mm});
            skArc(sketch, "E54.37.12.0", {"start": v(35.24, 9.44) * mm, "mid": v(34.29, 8.73) * mm, "end": v(34.1, 7.56) * mm});
            skLineSegment(sketch, "E54.41.12.0", {"start": v(38.93, 13.75) * mm, "end": v(39.12, 13.28) * mm});
            skArc(sketch, "E54.44.12.0", {"start": v(35.54, 14.58) * mm, "mid": v(35.22, 14.55) * mm, "end": v(34.91, 14.46) * mm});
            skArc(sketch, "E54.1.13.0", {"start": v(26.76, 22.45) * mm, "mid": v(27.8, 21.89) * mm, "end": v(28.94, 22.2) * mm});
            skLineSegment(sketch, "E54.4.13.0", {"start": v(29.98, 23) * mm, "end": v(28.94, 22.2) * mm});
            skPoint(sketch, "E54.7.13.0", {"position": v(30.23, 23.2) * mm});
            skArc(sketch, "E54.8.13.0", {"start": v(30.55, 23.28) * mm, "mid": v(32.1, 23.55) * mm, "end": v(33.68, 23.55) * mm});
            skPoint(sketch, "E54.12.13.0", {"position": v(33.9, 23.53) * mm});
            skPoint(sketch, "E54.13.13.0", {"position": v(33, 19.05) * mm});
            skLineSegment(sketch, "E54.14.13.0", {"start": v(32.73, 18.9) * mm, "end": v(31.6, 18.24) * mm});
            skArc(sketch, "E54.17.13.0", {"start": v(33.2, 19.32) * mm, "mid": v(34.04, 20.65) * mm, "end": v(34.65, 22.1) * mm});
            skPoint(sketch, "E54.21.13.0", {"position": v(34.72, 22.32) * mm});
            skArc(sketch, "E54.22.13.0", {"start": v(32.73, 18.9) * mm, "mid": v(32.99, 19.08) * mm, "end": v(33.2, 19.32) * mm});
            skArc(sketch, "E54.26.13.0", {"start": v(34.04, 23.36) * mm, "mid": v(33.88, 23.5) * mm, "end": v(33.68, 23.55) * mm});
            skLineSegment(sketch, "E54.30.13.0", {"start": v(34.6, 22.51) * mm, "end": v(34.35, 22.95) * mm});
            skArc(sketch, "E54.33.13.0", {"start": v(34.65, 22.1) * mm, "mid": v(34.67, 22.31) * mm, "end": v(34.6, 22.51) * mm});
            skArc(sketch, "E54.37.13.0", {"start": v(31.6, 18.24) * mm, "mid": v(30.86, 17.3) * mm, "end": v(30.98, 16.13) * mm});
            skLineSegment(sketch, "E54.41.13.0", {"start": v(34.04, 23.36) * mm, "end": v(34.35, 22.95) * mm});
            skArc(sketch, "E54.44.13.0", {"start": v(30.55, 23.28) * mm, "mid": v(30.25, 23.17) * mm, "end": v(29.98, 23) * mm});
            skArc(sketch, "E54.1.14.0", {"start": v(20.04, 28.6) * mm, "mid": v(21.19, 28.34) * mm, "end": v(22.2, 28.94) * mm});
            skLineSegment(sketch, "E54.4.14.0", {"start": v(23, 29.98) * mm, "end": v(22.2, 28.94) * mm});
            skPoint(sketch, "E54.7.14.0", {"position": v(23.2, 30.23) * mm});
            skArc(sketch, "E54.8.14.0", {"start": v(23.49, 30.4) * mm, "mid": v(24.92, 31.06) * mm, "end": v(26.44, 31.47) * mm});
            skPoint(sketch, "E54.12.14.0", {"position": v(26.66, 31.5) * mm});
            skPoint(sketch, "E54.13.14.0", {"position": v(26.94, 26.94) * mm});
            skLineSegment(sketch, "E54.14.14.0", {"start": v(26.72, 26.72) * mm, "end": v(25.8, 25.8) * mm});
            skArc(sketch, "E54.17.14.0", {"start": v(27.07, 27.25) * mm, "mid": v(27.54, 28.76) * mm, "end": v(27.75, 30.32) * mm});
            skPoint(sketch, "E54.21.14.0", {"position": v(27.76, 30.55) * mm});
            skArc(sketch, "E54.22.14.0", {"start": v(26.72, 26.72) * mm, "mid": v(26.92, 26.97) * mm, "end": v(27.07, 27.25) * mm});
            skArc(sketch, "E54.26.14.0", {"start": v(26.84, 31.37) * mm, "mid": v(26.65, 31.46) * mm, "end": v(26.44, 31.47) * mm});
            skLineSegment(sketch, "E54.30.14.0", {"start": v(27.6, 30.7) * mm, "end": v(27.24, 31.06) * mm});
            skArc(sketch, "E54.33.14.0", {"start": v(27.75, 30.32) * mm, "mid": v(27.72, 30.53) * mm, "end": v(27.6, 30.7) * mm});
            skArc(sketch, "E54.37.14.0", {"start": v(25.8, 25.8) * mm, "mid": v(25.33, 24.7) * mm, "end": v(25.75, 23.6) * mm});
            skLineSegment(sketch, "E54.41.14.0", {"start": v(26.84, 31.37) * mm, "end": v(27.24, 31.06) * mm});
            skArc(sketch, "E54.44.14.0", {"start": v(23.49, 30.4) * mm, "mid": v(23.22, 30.21) * mm, "end": v(23, 29.98) * mm});
            skArc(sketch, "E54.1.15.0", {"start": v(11.95, 32.82) * mm, "mid": v(13.13, 32.86) * mm, "end": v(13.96, 33.7) * mm});
            skLineSegment(sketch, "E54.4.15.0", {"start": v(14.46, 34.91) * mm, "end": v(13.96, 33.7) * mm});
            skPoint(sketch, "E54.7.15.0", {"position": v(14.58, 35.2) * mm});
            skArc(sketch, "E54.8.15.0", {"start": v(14.82, 35.44) * mm, "mid": v(16.03, 36.45) * mm, "end": v(17.4, 37.24) * mm});
            skPoint(sketch, "E54.12.15.0", {"position": v(17.6, 37.33) * mm});
            skPoint(sketch, "E54.13.15.0", {"position": v(19.05, 33) * mm});
            skLineSegment(sketch, "E54.14.15.0", {"start": v(18.9, 32.73) * mm, "end": v(18.24, 31.6) * mm});
            skArc(sketch, "E54.17.15.0", {"start": v(19.1, 33.33) * mm, "mid": v(19.16, 34.9) * mm, "end": v(18.96, 36.47) * mm});
            skPoint(sketch, "E54.21.15.0", {"position": v(18.9, 36.7) * mm});
            skArc(sketch, "E54.22.15.0", {"start": v(18.9, 32.73) * mm, "mid": v(19.03, 33.02) * mm, "end": v(19.1, 33.33) * mm});
            skArc(sketch, "E54.26.15.0", {"start": v(17.8, 37.25) * mm, "mid": v(17.6, 37.29) * mm, "end": v(17.4, 37.24) * mm});
            skLineSegment(sketch, "E54.30.15.0", {"start": v(18.71, 36.8) * mm, "end": v(18.27, 37.06) * mm});
            skArc(sketch, "E54.33.15.0", {"start": v(18.96, 36.47) * mm, "mid": v(18.87, 36.66) * mm, "end": v(18.71, 36.8) * mm});
            skArc(sketch, "E54.37.15.0", {"start": v(18.24, 31.6) * mm, "mid": v(18.07, 30.42) * mm, "end": v(18.76, 29.46) * mm});
            skLineSegment(sketch, "E54.41.15.0", {"start": v(17.8, 37.25) * mm, "end": v(18.27, 37.06) * mm});
            skArc(sketch, "E54.44.15.0", {"start": v(14.82, 35.44) * mm, "mid": v(14.61, 35.2) * mm, "end": v(14.46, 34.91) * mm});
            skArc(sketch, "E54.1.16.0", {"start": v(3.05, 34.8) * mm, "mid": v(4.18, 35.13) * mm, "end": v(4.76, 36.17) * mm});
            skLineSegment(sketch, "E54.4.16.0", {"start": v(4.93, 37.47) * mm, "end": v(4.76, 36.17) * mm});
            skPoint(sketch, "E54.7.16.0", {"position": v(4.97, 37.77) * mm});
            skArc(sketch, "E54.8.16.0", {"start": v(5.14, 38.07) * mm, "mid": v(6.05, 39.35) * mm, "end": v(7.16, 40.47) * mm});
            skPoint(sketch, "E54.12.16.0", {"position": v(7.34, 40.62) * mm});
            skPoint(sketch, "E54.13.16.0", {"position": v(9.86, 36.8) * mm});
            skLineSegment(sketch, "E54.14.16.0", {"start": v(9.78, 36.5) * mm, "end": v(9.44, 35.24) * mm});
            skArc(sketch, "E54.17.16.0", {"start": v(9.82, 37.14) * mm, "mid": v(9.47, 38.67) * mm, "end": v(8.87, 40.13) * mm});
            skPoint(sketch, "E54.21.16.0", {"position": v(8.77, 40.33) * mm});
            skArc(sketch, "E54.22.16.0", {"start": v(9.78, 36.5) * mm, "mid": v(9.83, 36.82) * mm, "end": v(9.82, 37.14) * mm});
            skArc(sketch, "E54.26.16.0", {"start": v(7.56, 40.59) * mm, "mid": v(7.35, 40.57) * mm, "end": v(7.16, 40.47) * mm});
            skLineSegment(sketch, "E54.30.16.0", {"start": v(8.55, 40.4) * mm, "end": v(8.06, 40.52) * mm});
            skArc(sketch, "E54.33.16.0", {"start": v(8.87, 40.13) * mm, "mid": v(8.74, 40.3) * mm, "end": v(8.55, 40.4) * mm});
            skArc(sketch, "E54.37.16.0", {"start": v(9.44, 35.24) * mm, "mid": v(9.58, 34.06) * mm, "end": v(10.5, 33.31) * mm});
            skLineSegment(sketch, "E54.41.16.0", {"start": v(7.56, 40.59) * mm, "end": v(8.06, 40.52) * mm});
            skArc(sketch, "E54.44.16.0", {"start": v(5.14, 38.07) * mm, "mid": v(5, 37.78) * mm, "end": v(4.93, 37.47) * mm});
            skArc(sketch, "E54.1.17.0", {"start": v(-6.06, 34.4) * mm, "mid": v(-5.06, 35.02) * mm, "end": v(-4.76, 36.17) * mm});
            skLineSegment(sketch, "E54.4.17.0", {"start": v(-4.93, 37.47) * mm, "end": v(-4.76, 36.17) * mm});
            skPoint(sketch, "E54.7.17.0", {"position": v(-4.97, 37.77) * mm});
            skArc(sketch, "E54.8.17.0", {"start": v(-4.89, 38.1) * mm, "mid": v(-4.34, 39.58) * mm, "end": v(-3.56, 40.95) * mm});
            skPoint(sketch, "E54.12.17.0", {"position": v(-3.43, 41.13) * mm});
            skPoint(sketch, "E54.13.17.0", {"position": v(0, 38.1) * mm});
            skLineSegment(sketch, "E54.14.17.0", {"start": v(0, 37.8) * mm, "end": v(0, 36.48) * mm});
            skArc(sketch, "E54.17.17.0", {"start": v(-0.13, 38.41) * mm, "mid": v(-0.86, 39.8) * mm, "end": v(-1.82, 41.06) * mm});
            skPoint(sketch, "E54.21.17.0", {"position": v(-1.97, 41.23) * mm});
            skArc(sketch, "E54.22.17.0", {"start": v(0, 37.8) * mm, "mid": v(-0.03, 38.1) * mm, "end": v(-0.13, 38.41) * mm});
            skArc(sketch, "E54.26.17.0", {"start": v(-3.2, 41.16) * mm, "mid": v(-3.4, 41.1) * mm, "end": v(-3.56, 40.95) * mm});
            skLineSegment(sketch, "E54.30.17.0", {"start": v(-2.2, 41.23) * mm, "end": v(-2.7, 41.23) * mm});
            skArc(sketch, "E54.33.17.0", {"start": v(-1.82, 41.06) * mm, "mid": v(-1.99, 41.18) * mm, "end": v(-2.2, 41.23) * mm});
            skArc(sketch, "E54.37.17.0", {"start": v(0, 36.48) * mm, "mid": v(0.44, 35.38) * mm, "end": v(1.52, 34.9) * mm});
            skLineSegment(sketch, "E54.41.17.0", {"start": v(-3.2, 41.16) * mm, "end": v(-2.7, 41.23) * mm});
            skArc(sketch, "E54.44.17.0", {"start": v(-4.89, 38.1) * mm, "mid": v(-4.94, 37.79) * mm, "end": v(-4.93, 37.47) * mm});
            skArc(sketch, "E54.1.18.0", {"start": v(-14.76, 31.65) * mm, "mid": v(-13.95, 32.52) * mm, "end": v(-13.96, 33.7) * mm});
            skLineSegment(sketch, "E54.4.18.0", {"start": v(-14.46, 34.91) * mm, "end": v(-13.96, 33.7) * mm});
            skPoint(sketch, "E54.7.18.0", {"position": v(-14.58, 35.2) * mm});
            skArc(sketch, "E54.8.18.0", {"start": v(-14.58, 35.54) * mm, "mid": v(-14.44, 37.1) * mm, "end": v(-14.03, 38.63) * mm});
            skPoint(sketch, "E54.12.18.0", {"position": v(-13.96, 38.84) * mm});
            skPoint(sketch, "E54.13.18.0", {"position": v(-9.86, 36.8) * mm});
            skLineSegment(sketch, "E54.14.18.0", {"start": v(-9.78, 36.5) * mm, "end": v(-9.44, 35.24) * mm});
            skArc(sketch, "E54.17.18.0", {"start": v(-10.06, 37.07) * mm, "mid": v(-11.14, 38.23) * mm, "end": v(-12.38, 39.2) * mm});
            skPoint(sketch, "E54.21.18.0", {"position": v(-12.58, 39.31) * mm});
            skArc(sketch, "E54.22.18.0", {"start": v(-9.78, 36.5) * mm, "mid": v(-9.9, 36.8) * mm, "end": v(-10.06, 37.07) * mm});
            skArc(sketch, "E54.26.18.0", {"start": v(-13.75, 38.93) * mm, "mid": v(-13.92, 38.8) * mm, "end": v(-14.03, 38.63) * mm});
            skLineSegment(sketch, "E54.30.18.0", {"start": v(-12.79, 39.26) * mm, "end": v(-13.28, 39.12) * mm});
            skArc(sketch, "E54.33.18.0", {"start": v(-12.38, 39.2) * mm, "mid": v(-12.58, 39.27) * mm, "end": v(-12.79, 39.26) * mm});
            skArc(sketch, "E54.37.18.0", {"start": v(-9.44, 35.24) * mm, "mid": v(-8.73, 34.29) * mm, "end": v(-7.56, 34.1) * mm});
            skLineSegment(sketch, "E54.41.18.0", {"start": v(-13.75, 38.93) * mm, "end": v(-13.28, 39.12) * mm});
            skArc(sketch, "E54.44.18.0", {"start": v(-14.58, 35.54) * mm, "mid": v(-14.55, 35.22) * mm, "end": v(-14.46, 34.91) * mm});
            skArc(sketch, "E54.1.19.0", {"start": v(-22.45, 26.76) * mm, "mid": v(-21.89, 27.8) * mm, "end": v(-22.2, 28.94) * mm});
            skLineSegment(sketch, "E54.4.19.0", {"start": v(-23, 29.98) * mm, "end": v(-22.2, 28.94) * mm});
            skPoint(sketch, "E54.7.19.0", {"position": v(-23.2, 30.23) * mm});
            skArc(sketch, "E54.8.19.0", {"start": v(-23.28, 30.55) * mm, "mid": v(-23.55, 32.1) * mm, "end": v(-23.55, 33.68) * mm});
            skPoint(sketch, "E54.12.19.0", {"position": v(-23.53, 33.9) * mm});
            skPoint(sketch, "E54.13.19.0", {"position": v(-19.05, 33) * mm});
            skLineSegment(sketch, "E54.14.19.0", {"start": v(-18.9, 32.73) * mm, "end": v(-18.24, 31.6) * mm});
            skArc(sketch, "E54.17.19.0", {"start": v(-19.32, 33.2) * mm, "mid": v(-20.65, 34.04) * mm, "end": v(-22.1, 34.65) * mm});
            skPoint(sketch, "E54.21.19.0", {"position": v(-22.32, 34.72) * mm});
            skArc(sketch, "E54.22.19.0", {"start": v(-18.9, 32.73) * mm, "mid": v(-19.08, 32.99) * mm, "end": v(-19.32, 33.2) * mm});
            skArc(sketch, "E54.26.19.0", {"start": v(-23.36, 34.04) * mm, "mid": v(-23.5, 33.88) * mm, "end": v(-23.55, 33.68) * mm});
            skLineSegment(sketch, "E54.30.19.0", {"start": v(-22.51, 34.6) * mm, "end": v(-22.95, 34.35) * mm});
            skArc(sketch, "E54.33.19.0", {"start": v(-22.1, 34.65) * mm, "mid": v(-22.31, 34.67) * mm, "end": v(-22.51, 34.6) * mm});
            skArc(sketch, "E54.37.19.0", {"start": v(-18.24, 31.6) * mm, "mid": v(-17.3, 30.86) * mm, "end": v(-16.13, 30.98) * mm});
            skLineSegment(sketch, "E54.41.19.0", {"start": v(-23.36, 34.04) * mm, "end": v(-22.95, 34.35) * mm});
            skArc(sketch, "E54.44.19.0", {"start": v(-23.28, 30.55) * mm, "mid": v(-23.17, 30.25) * mm, "end": v(-23, 29.98) * mm});
            skArc(sketch, "E54.1.20.0", {"start": v(-28.6, 20.04) * mm, "mid": v(-28.34, 21.19) * mm, "end": v(-28.94, 22.2) * mm});
            skLineSegment(sketch, "E54.4.20.0", {"start": v(-29.98, 23) * mm, "end": v(-28.94, 22.2) * mm});
            skPoint(sketch, "E54.7.20.0", {"position": v(-30.23, 23.2) * mm});
            skArc(sketch, "E54.8.20.0", {"start": v(-30.4, 23.49) * mm, "mid": v(-31.06, 24.92) * mm, "end": v(-31.47, 26.44) * mm});
            skPoint(sketch, "E54.12.20.0", {"position": v(-31.5, 26.66) * mm});
            skPoint(sketch, "E54.13.20.0", {"position": v(-26.94, 26.94) * mm});
            skLineSegment(sketch, "E54.14.20.0", {"start": v(-26.72, 26.72) * mm, "end": v(-25.8, 25.8) * mm});
            skArc(sketch, "E54.17.20.0", {"start": v(-27.25, 27.07) * mm, "mid": v(-28.76, 27.54) * mm, "end": v(-30.32, 27.75) * mm});
            skPoint(sketch, "E54.21.20.0", {"position": v(-30.55, 27.76) * mm});
            skArc(sketch, "E54.22.20.0", {"start": v(-26.72, 26.72) * mm, "mid": v(-26.97, 26.92) * mm, "end": v(-27.25, 27.07) * mm});
            skArc(sketch, "E54.26.20.0", {"start": v(-31.37, 26.84) * mm, "mid": v(-31.46, 26.65) * mm, "end": v(-31.47, 26.44) * mm});
            skLineSegment(sketch, "E54.30.20.0", {"start": v(-30.7, 27.6) * mm, "end": v(-31.06, 27.24) * mm});
            skArc(sketch, "E54.33.20.0", {"start": v(-30.32, 27.75) * mm, "mid": v(-30.53, 27.72) * mm, "end": v(-30.7, 27.6) * mm});
            skArc(sketch, "E54.37.20.0", {"start": v(-25.8, 25.8) * mm, "mid": v(-24.7, 25.33) * mm, "end": v(-23.6, 25.75) * mm});
            skLineSegment(sketch, "E54.41.20.0", {"start": v(-31.37, 26.84) * mm, "end": v(-31.06, 27.24) * mm});
            skArc(sketch, "E54.44.20.0", {"start": v(-30.4, 23.49) * mm, "mid": v(-30.21, 23.22) * mm, "end": v(-29.98, 23) * mm});
            skArc(sketch, "E54.1.21.0", {"start": v(-32.82, 11.95) * mm, "mid": v(-32.86, 13.13) * mm, "end": v(-33.7, 13.96) * mm});
            skLineSegment(sketch, "E54.4.21.0", {"start": v(-34.91, 14.46) * mm, "end": v(-33.7, 13.96) * mm});
            skPoint(sketch, "E54.7.21.0", {"position": v(-35.2, 14.58) * mm});
            skArc(sketch, "E54.8.21.0", {"start": v(-35.44, 14.82) * mm, "mid": v(-36.45, 16.03) * mm, "end": v(-37.24, 17.4) * mm});
            skPoint(sketch, "E54.12.21.0", {"position": v(-37.33, 17.6) * mm});
            skPoint(sketch, "E54.13.21.0", {"position": v(-33, 19.05) * mm});
            skLineSegment(sketch, "E54.14.21.0", {"start": v(-32.73, 18.9) * mm, "end": v(-31.6, 18.24) * mm});
            skArc(sketch, "E54.17.21.0", {"start": v(-33.33, 19.1) * mm, "mid": v(-34.9, 19.16) * mm, "end": v(-36.47, 18.96) * mm});
            skPoint(sketch, "E54.21.21.0", {"position": v(-36.7, 18.9) * mm});
            skArc(sketch, "E54.22.21.0", {"start": v(-32.73, 18.9) * mm, "mid": v(-33.02, 19.03) * mm, "end": v(-33.33, 19.1) * mm});
            skArc(sketch, "E54.26.21.0", {"start": v(-37.25, 17.8) * mm, "mid": v(-37.29, 17.6) * mm, "end": v(-37.24, 17.4) * mm});
            skLineSegment(sketch, "E54.30.21.0", {"start": v(-36.8, 18.71) * mm, "end": v(-37.06, 18.27) * mm});
            skArc(sketch, "E54.33.21.0", {"start": v(-36.47, 18.96) * mm, "mid": v(-36.66, 18.87) * mm, "end": v(-36.8, 18.71) * mm});
            skArc(sketch, "E54.37.21.0", {"start": v(-31.6, 18.24) * mm, "mid": v(-30.42, 18.07) * mm, "end": v(-29.46, 18.76) * mm});
            skLineSegment(sketch, "E54.41.21.0", {"start": v(-37.25, 17.8) * mm, "end": v(-37.06, 18.27) * mm});
            skArc(sketch, "E54.44.21.0", {"start": v(-35.44, 14.82) * mm, "mid": v(-35.2, 14.61) * mm, "end": v(-34.91, 14.46) * mm});
            skArc(sketch, "E54.1.22.0", {"start": v(-34.8, 3.05) * mm, "mid": v(-35.13, 4.18) * mm, "end": v(-36.17, 4.76) * mm});
            skLineSegment(sketch, "E54.4.22.0", {"start": v(-37.47, 4.93) * mm, "end": v(-36.17, 4.76) * mm});
            skPoint(sketch, "E54.7.22.0", {"position": v(-37.77, 4.97) * mm});
            skArc(sketch, "E54.8.22.0", {"start": v(-38.07, 5.14) * mm, "mid": v(-39.35, 6.05) * mm, "end": v(-40.47, 7.16) * mm});
            skPoint(sketch, "E54.12.22.0", {"position": v(-40.62, 7.34) * mm});
            skPoint(sketch, "E54.13.22.0", {"position": v(-36.8, 9.86) * mm});
            skLineSegment(sketch, "E54.14.22.0", {"start": v(-36.5, 9.78) * mm, "end": v(-35.24, 9.44) * mm});
            skArc(sketch, "E54.17.22.0", {"start": v(-37.14, 9.82) * mm, "mid": v(-38.67, 9.47) * mm, "end": v(-40.13, 8.87) * mm});
            skPoint(sketch, "E54.21.22.0", {"position": v(-40.33, 8.77) * mm});
            skArc(sketch, "E54.22.22.0", {"start": v(-36.5, 9.78) * mm, "mid": v(-36.82, 9.83) * mm, "end": v(-37.14, 9.82) * mm});
            skArc(sketch, "E54.26.22.0", {"start": v(-40.59, 7.56) * mm, "mid": v(-40.57, 7.35) * mm, "end": v(-40.47, 7.16) * mm});
            skLineSegment(sketch, "E54.30.22.0", {"start": v(-40.4, 8.55) * mm, "end": v(-40.52, 8.06) * mm});
            skArc(sketch, "E54.33.22.0", {"start": v(-40.13, 8.87) * mm, "mid": v(-40.3, 8.74) * mm, "end": v(-40.4, 8.55) * mm});
            skArc(sketch, "E54.37.22.0", {"start": v(-35.24, 9.44) * mm, "mid": v(-34.06, 9.58) * mm, "end": v(-33.31, 10.5) * mm});
            skLineSegment(sketch, "E54.41.22.0", {"start": v(-40.59, 7.56) * mm, "end": v(-40.52, 8.06) * mm});
            skArc(sketch, "E54.44.22.0", {"start": v(-38.07, 5.14) * mm, "mid": v(-37.78, 5) * mm, "end": v(-37.47, 4.93) * mm});
            skArc(sketch, "E54.1.23.0", {"start": v(-34.4, -6.06) * mm, "mid": v(-35.02, -5.06) * mm, "end": v(-36.17, -4.76) * mm});
            skLineSegment(sketch, "E54.4.23.0", {"start": v(-37.47, -4.93) * mm, "end": v(-36.17, -4.76) * mm});
            skPoint(sketch, "E54.7.23.0", {"position": v(-37.77, -4.97) * mm});
            skArc(sketch, "E54.8.23.0", {"start": v(-38.1, -4.89) * mm, "mid": v(-39.58, -4.34) * mm, "end": v(-40.95, -3.56) * mm});
            skPoint(sketch, "E54.12.23.0", {"position": v(-41.13, -3.43) * mm});
            skPoint(sketch, "E54.13.23.0", {"position": v(-38.1, 0) * mm});
            skLineSegment(sketch, "E54.14.23.0", {"start": v(-37.8, 0) * mm, "end": v(-36.48, 0) * mm});
            skArc(sketch, "E54.17.23.0", {"start": v(-38.41, -0.13) * mm, "mid": v(-39.8, -0.86) * mm, "end": v(-41.06, -1.82) * mm});
            skPoint(sketch, "E54.21.23.0", {"position": v(-41.23, -1.97) * mm});
            skArc(sketch, "E54.22.23.0", {"start": v(-37.8, 0) * mm, "mid": v(-38.1, -0.03) * mm, "end": v(-38.41, -0.13) * mm});
            skArc(sketch, "E54.26.23.0", {"start": v(-41.16, -3.2) * mm, "mid": v(-41.1, -3.4) * mm, "end": v(-40.95, -3.56) * mm});
            skLineSegment(sketch, "E54.30.23.0", {"start": v(-41.23, -2.2) * mm, "end": v(-41.23, -2.7) * mm});
            skArc(sketch, "E54.33.23.0", {"start": v(-41.06, -1.82) * mm, "mid": v(-41.18, -1.99) * mm, "end": v(-41.23, -2.2) * mm});
            skArc(sketch, "E54.37.23.0", {"start": v(-36.48, 0) * mm, "mid": v(-35.38, 0.44) * mm, "end": v(-34.9, 1.52) * mm});
            skLineSegment(sketch, "E54.41.23.0", {"start": v(-41.16, -3.2) * mm, "end": v(-41.23, -2.7) * mm});
            skArc(sketch, "E54.44.23.0", {"start": v(-38.1, -4.89) * mm, "mid": v(-37.79, -4.94) * mm, "end": v(-37.47, -4.93) * mm});
            skArc(sketch, "E55.trimOffspring", {"start": v(-34.4, -6.06) * mm, "mid": v(-34.25, -6.81) * mm, "end": v(-34.1, -7.56) * mm});
            skArc(sketch, "E56.trimOffspring", {"start": v(-34.8, 3.05) * mm, "mid": v(-34.85, 2.28) * mm, "end": v(-34.9, 1.52) * mm});
            skArc(sketch, "E57.trimOffspring", {"start": v(-32.82, 11.95) * mm, "mid": v(-33.07, 11.23) * mm, "end": v(-33.31, 10.5) * mm});
            skArc(sketch, "E58.trimOffspring", {"start": v(-28.6, 20.04) * mm, "mid": v(-29.04, 19.4) * mm, "end": v(-29.46, 18.76) * mm});
            skArc(sketch, "E59.trimOffspring", {"start": v(-22.45, 26.76) * mm, "mid": v(-23.03, 26.26) * mm, "end": v(-23.6, 25.75) * mm});
            skArc(sketch, "E60.trimOffspring", {"start": v(-14.76, 31.65) * mm, "mid": v(-15.45, 31.32) * mm, "end": v(-16.13, 30.98) * mm});
            skArc(sketch, "E61.trimOffspring", {"start": v(-6.06, 34.4) * mm, "mid": v(-6.81, 34.25) * mm, "end": v(-7.56, 34.1) * mm});
            skArc(sketch, "E62.trimOffspring", {"start": v(3.05, 34.8) * mm, "mid": v(2.28, 34.85) * mm, "end": v(1.52, 34.9) * mm});
            skArc(sketch, "E63.trimOffspring", {"start": v(11.95, 32.82) * mm, "mid": v(11.23, 33.07) * mm, "end": v(10.5, 33.31) * mm});
            skArc(sketch, "E64.trimOffspring", {"start": v(20.04, 28.6) * mm, "mid": v(19.4, 29.04) * mm, "end": v(18.76, 29.46) * mm});
            skArc(sketch, "E65.trimOffspring", {"start": v(26.76, 22.45) * mm, "mid": v(26.26, 23.03) * mm, "end": v(25.75, 23.6) * mm});
            skArc(sketch, "E66.trimOffspring", {"start": v(31.65, 14.76) * mm, "mid": v(31.32, 15.45) * mm, "end": v(30.98, 16.13) * mm});
            skArc(sketch, "E67.trimOffspring", {"start": v(34.4, 6.06) * mm, "mid": v(34.25, 6.81) * mm, "end": v(34.1, 7.56) * mm});
            skArc(sketch, "E68.trimOffspring", {"start": v(34.8, -3.05) * mm, "mid": v(34.85, -2.28) * mm, "end": v(34.9, -1.52) * mm});
            skArc(sketch, "E69.trimOffspring", {"start": v(32.82, -11.95) * mm, "mid": v(33.07, -11.23) * mm, "end": v(33.31, -10.5) * mm});
            skArc(sketch, "E70.trimOffspring", {"start": v(28.6, -20.04) * mm, "mid": v(29.04, -19.4) * mm, "end": v(29.46, -18.76) * mm});
            skArc(sketch, "E71.trimOffspring", {"start": v(14.76, -31.65) * mm, "mid": v(15.45, -31.32) * mm, "end": v(16.13, -30.98) * mm});
            skArc(sketch, "E72.trimOffspring", {"start": v(22.45, -26.76) * mm, "mid": v(23.03, -26.26) * mm, "end": v(23.6, -25.75) * mm});
            skArc(sketch, "E73.trimOffspring", {"start": v(6.06, -34.4) * mm, "mid": v(6.81, -34.25) * mm, "end": v(7.56, -34.1) * mm});
            skArc(sketch, "E74.trimOffspring", {"start": v(-3.05, -34.8) * mm, "mid": v(-2.28, -34.85) * mm, "end": v(-1.52, -34.9) * mm});
            skArc(sketch, "E75.trimOffspring", {"start": v(-11.95, -32.82) * mm, "mid": v(-11.23, -33.07) * mm, "end": v(-10.5, -33.31) * mm});
            skArc(sketch, "E76.trimOffspring", {"start": v(-20.04, -28.6) * mm, "mid": v(-19.4, -29.04) * mm, "end": v(-18.76, -29.46) * mm});
            skArc(sketch, "E77.trimOffspring", {"start": v(-26.76, -22.45) * mm, "mid": v(-26.26, -23.03) * mm, "end": v(-25.75, -23.6) * mm});
            skLineSegment(sketch, "E78", {"start": v(0, 0) * mm, "end": v(3, -11.17) * mm});
            skSolve(sketch);
        }
        {
            var Q0;
            Q0=makeQuery(id+"F1.imprint","IMPRINT",FACE,{"disambiguationData":[TD([[makeQuery(id+"F1.imprint","IMPRINT",EDGE,{"derivedFrom":sQuery(id+"F1.wireOp",EDGE,"E0")}),1.0]])]});
            var Q1;
            Q1=makeQuery(id+"F2.imprint","IMPRINT",FACE,{"disambiguationData":[TD([[makeQuery(id+"F2.imprint","IMPRINT",EDGE,{"derivedFrom":sQuery(id+"F2.wireOp",EDGE,"E39")}),1.0]])]});
            var Q2;
            Q2=sQuery(id+"F1.wireOp",VERTEX,"E4.MirrorCS.end");
            var Q3;
            Q3=sQuery(id+"F2.wireOp",VERTEX,"E54.41.16.0.end");
            loft(context, id + "F3", {"sheetProfilesArray" : [{ "sheetProfileEntities" : qUnion([Q0]) }, { "sheetProfileEntities" : qUnion([Q1]) }], "matchConnections" : true, "connections" : [{ "connectionEntities" : qUnion([Q2, Q3]), "connectionEdgeQueries" : qUnion([]), "connectionEdgeParameters" : [] }]});
        }
        {
            var Q0;
            Q0=sQuery(id+"F2.wireOp",VERTEX,"E39.center");
            var Q1;
            Q1=makeQuery(id+"F3.opLoft","SWEPT_BODY",BODY,{"disambiguationData":[OSD([makeQuery(id+"F1.imprint","IMPRINT",FACE,{"disambiguationData":[TD([[makeQuery(id+"F1.imprint","IMPRINT",EDGE,{"derivedFrom":sQuery(id+"F1.wireOp",EDGE,"E0")}),1.0]])]}),makeQuery(id+"F2.imprint","IMPRINT",FACE,{"disambiguationData":[TD([[makeQuery(id+"F2.imprint","IMPRINT",EDGE,{"derivedFrom":sQuery(id+"F2.wireOp",EDGE,"E39")}),1.0]])]})])]});
            hole(context, id + "F4", {"style" : HoleStyle.SIMPLE, "endStyle" : HoleEndStyle.THROUGH, "holeDiameter" : 12.7 * mm, "tappedDepth" : 12.7 * mm, "tapClearance" : 3, "locations" : qUnion([Q0]), "scope" : qUnion([Q1])});
        }
    });
